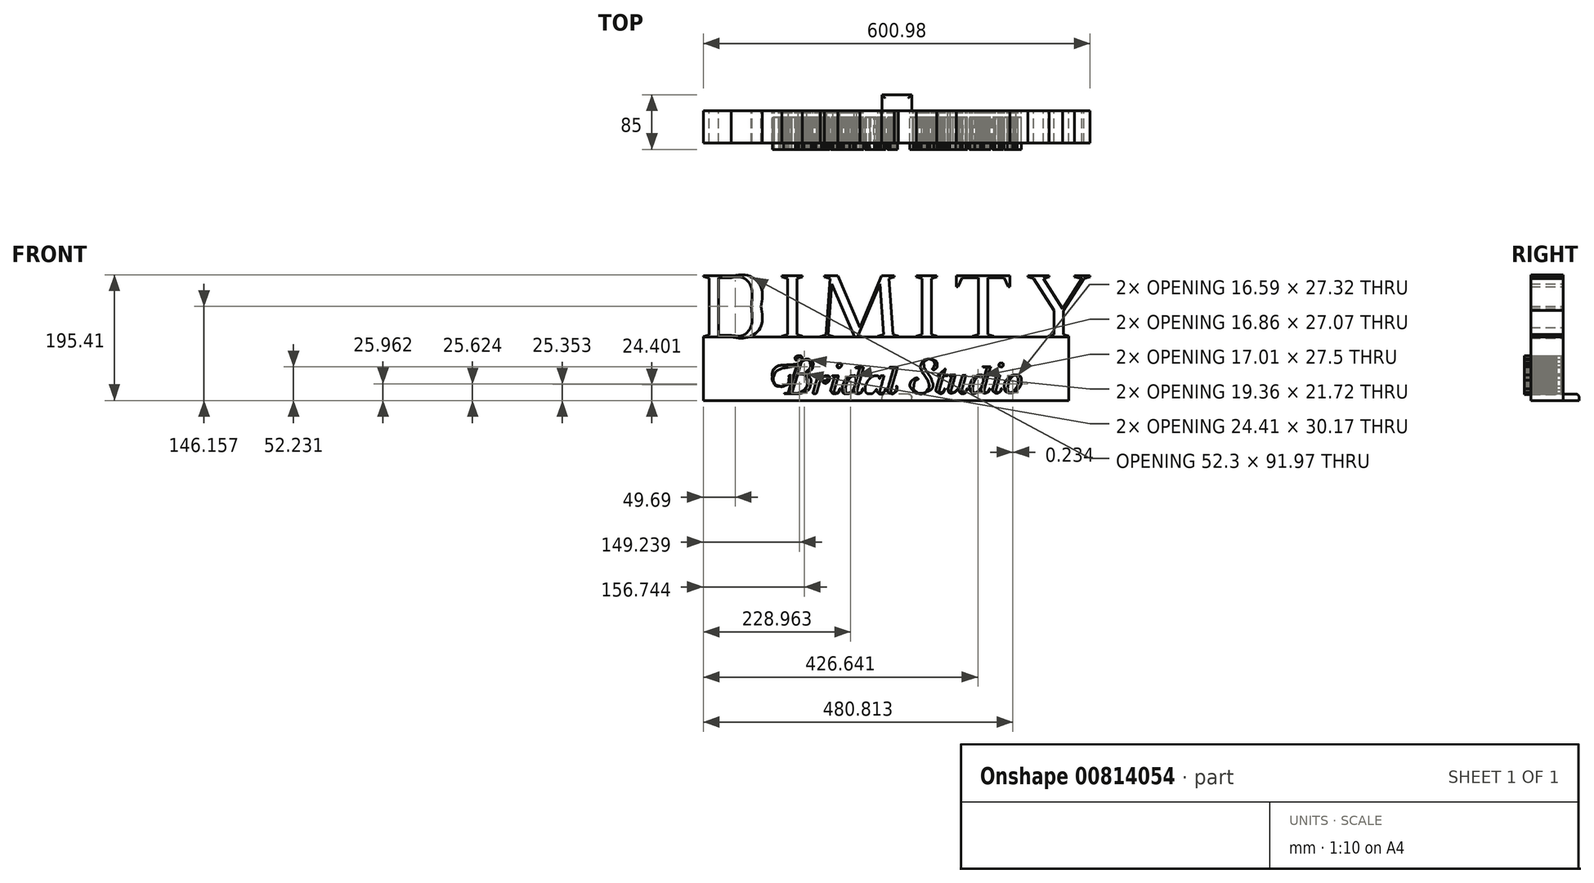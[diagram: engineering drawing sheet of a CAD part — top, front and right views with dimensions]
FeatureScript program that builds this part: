
annotation { "Feature Type Name" : "Feature", "Feature Type Description" : "" }
export const myFeature = defineFeature(function(context is Context, id is Id, definition is map)
    precondition{}
    {
        {
            var Q0;
            Q0=qCreatedBy(makeId("Front.planeOp"),FACE);
            var sketch = newSketch(context, id + "F0", { "sketchPlane" : qUnion([Q0])});
            skLineSegment(sketch, "E0", {"start": v(-300.49, 107.52) * mm, "end": v(-300.49, 106.3) * mm});
            skLineSegment(sketch, "E1", {"start": v(-300.49, 106.3) * mm, "end": v(-291.64, 104.26) * mm});
            skLineSegment(sketch, "E2", {"start": v(-291.64, 104.26) * mm, "end": v(-291.64, 15.55) * mm});
            skLineSegment(sketch, "E3", {"start": v(-291.64, 15.55) * mm, "end": v(-300.49, 13.37) * mm});
            skLineSegment(sketch, "E4", {"start": v(-300.49, 13.37) * mm, "end": v(-300.49, 12.28) * mm});
            skLineSegment(sketch, "E5", {"start": v(-300.49, 12.28) * mm, "end": v(-257.09, 12.28) * mm});
            skFitSpline(sketch, "E6", {"points": [v(-257.09, 12.28) * mm, v(-229.88, 12.28) * mm, v(-210.83, 29.97) * mm, v(-210.83, 59.9) * mm]});
            skFitSpline(sketch, "E7", {"points": [v(-210.83, 59.9) * mm, v(-210.83, 89.56) * mm, v(-229.88, 107.52) * mm, v(-257.09, 107.52) * mm]});
            skLineSegment(sketch, "E8", {"start": v(-257.09, 107.52) * mm, "end": v(-300.49, 107.52) * mm});
            skLineSegment(sketch, "E9", {"start": v(-276.95, 104.8) * mm, "end": v(-257.09, 104.8) * mm});
            skFitSpline(sketch, "E10", {"points": [v(-257.09, 104.8) * mm, v(-239.13, 104.8) * mm, v(-226.2, 89.83) * mm, v(-226.2, 59.77) * mm]});
            skFitSpline(sketch, "E11", {"points": [v(-226.2, 59.77) * mm, v(-226.2, 29.84) * mm, v(-239.13, 15) * mm, v(-257.09, 15) * mm]});
            skLineSegment(sketch, "E12", {"start": v(-257.09, 15) * mm, "end": v(-276.95, 15) * mm});
            skLineSegment(sketch, "E13", {"start": v(-276.95, 15) * mm, "end": v(-276.95, 104.8) * mm});
            skLineSegment(sketch, "E14", {"start": v(-178.44, 107.52) * mm, "end": v(-178.44, 106.16) * mm});
            skLineSegment(sketch, "E15", {"start": v(-178.44, 106.16) * mm, "end": v(-169.6, 103.58) * mm});
            skLineSegment(sketch, "E16", {"start": v(-169.6, 103.58) * mm, "end": v(-169.6, 16.23) * mm});
            skLineSegment(sketch, "E17", {"start": v(-169.6, 16.23) * mm, "end": v(-178.44, 13.64) * mm});
            skLineSegment(sketch, "E18", {"start": v(-178.44, 13.64) * mm, "end": v(-178.44, 12.28) * mm});
            skLineSegment(sketch, "E19", {"start": v(-178.44, 12.28) * mm, "end": v(-146.74, 12.28) * mm});
            skLineSegment(sketch, "E20", {"start": v(-146.74, 12.28) * mm, "end": v(-146.74, 13.64) * mm});
            skLineSegment(sketch, "E21", {"start": v(-146.74, 13.64) * mm, "end": v(-155.17, 16.23) * mm});
            skLineSegment(sketch, "E22", {"start": v(-155.17, 16.23) * mm, "end": v(-155.17, 103.58) * mm});
            skLineSegment(sketch, "E23", {"start": v(-155.17, 103.58) * mm, "end": v(-146.74, 106.16) * mm});
            skLineSegment(sketch, "E24", {"start": v(-146.74, 106.16) * mm, "end": v(-146.74, 107.52) * mm});
            skLineSegment(sketch, "E25", {"start": v(-146.74, 107.52) * mm, "end": v(-178.44, 107.52) * mm});
            skLineSegment(sketch, "E26", {"start": v(-112.18, 107.52) * mm, "end": v(-112.18, 106.16) * mm});
            skLineSegment(sketch, "E27", {"start": v(-112.18, 106.16) * mm, "end": v(-103.34, 103.58) * mm});
            skLineSegment(sketch, "E28", {"start": v(-103.34, 103.58) * mm, "end": v(-109.73, 15.96) * mm});
            skLineSegment(sketch, "E29", {"start": v(-109.73, 15.96) * mm, "end": v(-118.57, 13.37) * mm});
            skLineSegment(sketch, "E30", {"start": v(-118.57, 13.37) * mm, "end": v(-118.57, 12.28) * mm});
            skLineSegment(sketch, "E31", {"start": v(-118.57, 12.28) * mm, "end": v(-98.57, 12.28) * mm});
            skLineSegment(sketch, "E32", {"start": v(-98.57, 12.28) * mm, "end": v(-98.57, 13.37) * mm});
            skLineSegment(sketch, "E33", {"start": v(-98.57, 13.37) * mm, "end": v(-106.88, 15.96) * mm});
            skLineSegment(sketch, "E34", {"start": v(-106.88, 15.96) * mm, "end": v(-101.02, 95.14) * mm});
            skLineSegment(sketch, "E35", {"start": v(-101.02, 95.14) * mm, "end": v(-65.51, 12.28) * mm});
            skLineSegment(sketch, "E36", {"start": v(-65.51, 12.28) * mm, "end": v(-61.02, 12.28) * mm});
            skLineSegment(sketch, "E37", {"start": v(-61.02, 12.28) * mm, "end": v(-26.06, 95) * mm});
            skLineSegment(sketch, "E38", {"start": v(-26.06, 95) * mm, "end": v(-20.34, 16.23) * mm});
            skLineSegment(sketch, "E39", {"start": v(-20.34, 16.23) * mm, "end": v(-29.19, 13.64) * mm});
            skLineSegment(sketch, "E40", {"start": v(-29.19, 13.64) * mm, "end": v(-29.19, 12.28) * mm});
            skLineSegment(sketch, "E41", {"start": v(-29.19, 12.28) * mm, "end": v(2.65, 12.28) * mm});
            skLineSegment(sketch, "E42", {"start": v(2.65, 12.28) * mm, "end": v(2.65, 13.64) * mm});
            skLineSegment(sketch, "E43", {"start": v(2.65, 13.64) * mm, "end": v(-5.79, 16.23) * mm});
            skLineSegment(sketch, "E44", {"start": v(-5.79, 16.23) * mm, "end": v(-12.04, 103.58) * mm});
            skLineSegment(sketch, "E45", {"start": v(-12.04, 103.58) * mm, "end": v(-3.6, 106.16) * mm});
            skLineSegment(sketch, "E46", {"start": v(-3.6, 106.16) * mm, "end": v(-3.6, 107.52) * mm});
            skLineSegment(sketch, "E47", {"start": v(-3.6, 107.52) * mm, "end": v(-23.6, 107.52) * mm});
            skLineSegment(sketch, "E48", {"start": v(-23.6, 107.52) * mm, "end": v(-57.35, 27.25) * mm});
            skLineSegment(sketch, "E49", {"start": v(-57.35, 27.25) * mm, "end": v(-91.36, 107.52) * mm});
            skLineSegment(sketch, "E50", {"start": v(-91.36, 107.52) * mm, "end": v(-112.18, 107.52) * mm});
            skLineSegment(sketch, "E51", {"start": v(30.55, 107.52) * mm, "end": v(30.55, 106.16) * mm});
            skLineSegment(sketch, "E52", {"start": v(30.55, 106.16) * mm, "end": v(39.4, 103.58) * mm});
            skLineSegment(sketch, "E53", {"start": v(39.4, 103.58) * mm, "end": v(39.4, 16.23) * mm});
            skLineSegment(sketch, "E54", {"start": v(39.4, 16.23) * mm, "end": v(30.55, 13.64) * mm});
            skLineSegment(sketch, "E55", {"start": v(30.55, 13.64) * mm, "end": v(30.55, 12.28) * mm});
            skLineSegment(sketch, "E56", {"start": v(30.55, 12.28) * mm, "end": v(62.25, 12.28) * mm});
            skLineSegment(sketch, "E57", {"start": v(62.25, 12.28) * mm, "end": v(62.25, 13.64) * mm});
            skLineSegment(sketch, "E58", {"start": v(62.25, 13.64) * mm, "end": v(53.81, 16.23) * mm});
            skLineSegment(sketch, "E59", {"start": v(53.81, 16.23) * mm, "end": v(53.81, 103.58) * mm});
            skLineSegment(sketch, "E60", {"start": v(53.81, 103.58) * mm, "end": v(62.25, 106.16) * mm});
            skLineSegment(sketch, "E61", {"start": v(62.25, 106.16) * mm, "end": v(62.25, 107.52) * mm});
            skLineSegment(sketch, "E62", {"start": v(62.25, 107.52) * mm, "end": v(30.55, 107.52) * mm});
            skLineSegment(sketch, "E63", {"start": v(93, 107.52) * mm, "end": v(93, 90.79) * mm});
            skLineSegment(sketch, "E64", {"start": v(93, 90.79) * mm, "end": v(95.17, 90.79) * mm});
            skLineSegment(sketch, "E65", {"start": v(95.17, 90.79) * mm, "end": v(101.57, 104.8) * mm});
            skLineSegment(sketch, "E66", {"start": v(101.57, 104.8) * mm, "end": v(126.88, 104.8) * mm});
            skLineSegment(sketch, "E67", {"start": v(126.88, 104.8) * mm, "end": v(126.88, 16.23) * mm});
            skLineSegment(sketch, "E68", {"start": v(126.88, 16.23) * mm, "end": v(118.03, 13.64) * mm});
            skLineSegment(sketch, "E69", {"start": v(118.03, 13.64) * mm, "end": v(118.03, 12.28) * mm});
            skLineSegment(sketch, "E70", {"start": v(118.03, 12.28) * mm, "end": v(150.41, 12.28) * mm});
            skLineSegment(sketch, "E71", {"start": v(150.41, 12.28) * mm, "end": v(150.41, 13.64) * mm});
            skLineSegment(sketch, "E72", {"start": v(150.41, 13.64) * mm, "end": v(141.57, 16.23) * mm});
            skLineSegment(sketch, "E73", {"start": v(141.57, 16.23) * mm, "end": v(141.57, 104.8) * mm});
            skLineSegment(sketch, "E74", {"start": v(141.57, 104.8) * mm, "end": v(167.01, 104.8) * mm});
            skLineSegment(sketch, "E75", {"start": v(167.01, 104.8) * mm, "end": v(173.27, 90.79) * mm});
            skLineSegment(sketch, "E76", {"start": v(173.27, 90.79) * mm, "end": v(175.58, 90.79) * mm});
            skLineSegment(sketch, "E77", {"start": v(175.58, 90.79) * mm, "end": v(175.58, 107.52) * mm});
            skLineSegment(sketch, "E78", {"start": v(175.58, 107.52) * mm, "end": v(93, 107.52) * mm});
            skLineSegment(sketch, "E79", {"start": v(204.16, 107.52) * mm, "end": v(204.16, 106.16) * mm});
            skLineSegment(sketch, "E80", {"start": v(204.16, 106.16) * mm, "end": v(212.6, 103.58) * mm});
            skLineSegment(sketch, "E81", {"start": v(212.6, 103.58) * mm, "end": v(244.43, 53.64) * mm});
            skLineSegment(sketch, "E82", {"start": v(244.43, 53.64) * mm, "end": v(244.43, 16.23) * mm});
            skLineSegment(sketch, "E83", {"start": v(244.43, 16.23) * mm, "end": v(235.6, 13.64) * mm});
            skLineSegment(sketch, "E84", {"start": v(235.6, 13.64) * mm, "end": v(235.6, 12.28) * mm});
            skLineSegment(sketch, "E85", {"start": v(235.6, 12.28) * mm, "end": v(267.43, 12.28) * mm});
            skLineSegment(sketch, "E86", {"start": v(267.43, 12.28) * mm, "end": v(267.43, 13.64) * mm});
            skLineSegment(sketch, "E87", {"start": v(267.43, 13.64) * mm, "end": v(259, 16.23) * mm});
            skLineSegment(sketch, "E88", {"start": v(259, 16.23) * mm, "end": v(259, 53.64) * mm});
            skLineSegment(sketch, "E89", {"start": v(259, 53.64) * mm, "end": v(290.83, 103.58) * mm});
            skLineSegment(sketch, "E90", {"start": v(290.83, 103.58) * mm, "end": v(300.49, 106.16) * mm});
            skLineSegment(sketch, "E91", {"start": v(300.49, 106.16) * mm, "end": v(300.49, 107.52) * mm});
            skLineSegment(sketch, "E92", {"start": v(300.49, 107.52) * mm, "end": v(276.27, 107.52) * mm});
            skLineSegment(sketch, "E93", {"start": v(276.27, 107.52) * mm, "end": v(276.27, 106.16) * mm});
            skLineSegment(sketch, "E94", {"start": v(276.27, 106.16) * mm, "end": v(287.7, 103.58) * mm});
            skLineSegment(sketch, "E95", {"start": v(287.7, 103.58) * mm, "end": v(257.63, 56.64) * mm});
            skLineSegment(sketch, "E96", {"start": v(257.63, 56.64) * mm, "end": v(227.97, 103.58) * mm});
            skLineSegment(sketch, "E97", {"start": v(227.97, 103.58) * mm, "end": v(236.95, 106.16) * mm});
            skLineSegment(sketch, "E98", {"start": v(236.95, 106.16) * mm, "end": v(236.95, 107.52) * mm});
            skLineSegment(sketch, "E99", {"start": v(236.95, 107.52) * mm, "end": v(204.16, 107.52) * mm});
            skFitSpline(sketch, "E100", {"points": [v(-152.8, -16.98) * mm, v(-153.04, -17) * mm, v(-153.29, -17.01) * mm, v(-153.54, -17.05) * mm]});
            skFitSpline(sketch, "E101", {"points": [v(-153.54, -17.05) * mm, v(-156.18, -17.4) * mm, v(-157.9, -19.88) * mm, v(-157.32, -22.49) * mm]});
            skFitSpline(sketch, "E102", {"points": [v(-157.32, -22.49) * mm, v(-157.17, -23.17) * mm, v(-156.84, -23.7) * mm, v(-156.02, -23.97) * mm]});
            skFitSpline(sketch, "E103", {"points": [v(-156.02, -23.97) * mm, v(-155.76, -23.3) * mm, v(-155.5, -22.7) * mm, v(-155.27, -22.1) * mm]});
            skFitSpline(sketch, "E104", {"points": [v(-155.27, -22.1) * mm, v(-154.62, -20.46) * mm, v(-153.4, -19.45) * mm, v(-151.72, -19.03) * mm]});
            skFitSpline(sketch, "E105", {"points": [v(-151.72, -19.03) * mm, v(-150.18, -18.63) * mm, v(-148.46, -19.17) * mm, v(-147.61, -21.44) * mm]});
            skFitSpline(sketch, "E106", {"points": [v(-147.61, -21.44) * mm, v(-147.29, -22.6) * mm, v(-147.43, -23.05) * mm, v(-147.61, -23.61) * mm]});
            skFitSpline(sketch, "E107", {"points": [v(-147.61, -23.61) * mm, v(-148.32, -25.33) * mm, v(-149.28, -26.65) * mm, v(-150.77, -27.59) * mm]});
            skFitSpline(sketch, "E108", {"points": [v(-150.77, -27.59) * mm, v(-152.75, -28.84) * mm, v(-154.93, -29.6) * mm, v(-157.2, -29.9) * mm]});
            skFitSpline(sketch, "E109", {"points": [v(-157.2, -29.9) * mm, v(-160.75, -30.36) * mm, v(-164.33, -30.69) * mm, v(-167.9, -30.82) * mm]});
            skFitSpline(sketch, "E110", {"points": [v(-167.9, -30.82) * mm, v(-170.73, -30.92) * mm, v(-173.52, -31.26) * mm, v(-176.32, -31.64) * mm]});
            skFitSpline(sketch, "E111", {"points": [v(-176.32, -31.64) * mm, v(-185.34, -32.84) * mm, v(-192.7, -40.76) * mm, v(-193.3, -49.28) * mm]});
            skFitSpline(sketch, "E112", {"points": [v(-193.3, -49.28) * mm, v(-193.53, -52.42) * mm, v(-193.13, -55.38) * mm, v(-191.65, -58.16) * mm]});
            skFitSpline(sketch, "E113", {"points": [v(-191.65, -58.16) * mm, v(-189.52, -62.19) * mm, v(-186.07, -64.19) * mm, v(-181.6, -64.51) * mm]});
            skFitSpline(sketch, "E114", {"points": [v(-181.6, -64.51) * mm, v(-178.73, -64.72) * mm, v(-175.97, -64.25) * mm, v(-173.32, -63.13) * mm]});
            skFitSpline(sketch, "E115", {"points": [v(-173.32, -63.13) * mm, v(-169.2, -61.37) * mm, v(-165.98, -58.67) * mm, v(-164.2, -54.46) * mm]});
            skFitSpline(sketch, "E116", {"points": [v(-164.2, -54.46) * mm, v(-163.5, -52.79) * mm, v(-163.26, -51.04) * mm, v(-163.84, -49.28) * mm]});
            skFitSpline(sketch, "E117", {"points": [v(-163.84, -49.28) * mm, v(-164.45, -47.46) * mm, v(-166.05, -46.95) * mm, v(-167.88, -48.07) * mm]});
            skFitSpline(sketch, "E118", {"points": [v(-167.88, -48.07) * mm, v(-167.12, -49.52) * mm, v(-167.24, -51.02) * mm, v(-167.36, -52.49) * mm]});
            skFitSpline(sketch, "E119", {"points": [v(-167.36, -52.49) * mm, v(-167.76, -57.27) * mm, v(-170.1, -60.76) * mm, v(-174.54, -62.72) * mm]});
            skFitSpline(sketch, "E120", {"points": [v(-174.54, -62.72) * mm, v(-177.39, -63.97) * mm, v(-180.37, -64.22) * mm, v(-183.39, -63.54) * mm]});
            skFitSpline(sketch, "E121", {"points": [v(-183.39, -63.54) * mm, v(-186.2, -62.9) * mm, v(-188.52, -61.45) * mm, v(-189.98, -58.87) * mm]});
            skFitSpline(sketch, "E122", {"points": [v(-189.98, -58.87) * mm, v(-191.95, -55.34) * mm, v(-192.08, -51.59) * mm, v(-190.71, -47.9) * mm]});
            skFitSpline(sketch, "E123", {"points": [v(-190.71, -47.9) * mm, v(-188.8, -42.75) * mm, v(-184.98, -39.31) * mm, v(-179.95, -37.17) * mm]});
            skFitSpline(sketch, "E124", {"points": [v(-179.95, -37.17) * mm, v(-176.52, -35.71) * mm, v(-172.82, -35.4) * mm, v(-169.22, -34.7) * mm]});
            skFitSpline(sketch, "E125", {"points": [v(-169.22, -34.7) * mm, v(-164.8, -33.83) * mm, v(-160.41, -32.95) * mm, v(-156.21, -31.29) * mm]});
            skFitSpline(sketch, "E126", {"points": [v(-156.21, -31.29) * mm, v(-155.8, -31.12) * mm, v(-155.35, -31.04) * mm, v(-154.74, -30.87) * mm]});
            skFitSpline(sketch, "E127", {"points": [v(-154.74, -30.87) * mm, v(-159.45, -45.8) * mm, v(-164.09, -60.51) * mm, v(-168.77, -75.36) * mm]});
            skFitSpline(sketch, "E128", {"points": [v(-168.77, -75.36) * mm, v(-169.81, -75.36) * mm, v(-170.81, -75.32) * mm, v(-171.8, -75.38) * mm]});
            skFitSpline(sketch, "E129", {"points": [v(-171.8, -75.38) * mm, v(-172.77, -75.43) * mm, v(-173.8, -75.1) * mm, v(-174.7, -75.79) * mm]});
            skFitSpline(sketch, "E130", {"points": [v(-174.7, -75.79) * mm, v(-174.18, -75.97) * mm, v(-173.67, -76) * mm, v(-173.16, -76) * mm]});
            skFitSpline(sketch, "E131", {"points": [v(-173.16, -76) * mm, v(-167.7, -76.01) * mm, v(-162.24, -76) * mm, v(-156.78, -76.01) * mm]});
            skFitSpline(sketch, "E132", {"points": [v(-156.78, -76.01) * mm, v(-154.43, -76.02) * mm, v(-152.1, -75.82) * mm, v(-149.84, -75.16) * mm]});
            skFitSpline(sketch, "E133", {"points": [v(-149.84, -75.16) * mm, v(-141.45, -72.71) * mm, v(-135.78, -67.59) * mm, v(-133.9, -58.82) * mm]});
            skFitSpline(sketch, "E134", {"points": [v(-133.9, -58.82) * mm, v(-133.28, -55.91) * mm, v(-133.76, -53.07) * mm, v(-135.3, -50.52) * mm]});
            skFitSpline(sketch, "E135", {"points": [v(-135.3, -50.52) * mm, v(-137.03, -47.7) * mm, v(-139.64, -46) * mm, v(-142.84, -45.2) * mm]});
            skFitSpline(sketch, "E136", {"points": [v(-142.84, -45.2) * mm, v(-143.45, -45.04) * mm, v(-144.06, -44.9) * mm, v(-144.67, -44.77) * mm]});
            skFitSpline(sketch, "E137", {"points": [v(-144.67, -44.77) * mm, v(-141.88, -43.95) * mm, v(-139.26, -42.96) * mm, v(-136.88, -41.38) * mm]});
            skFitSpline(sketch, "E138", {"points": [v(-136.88, -41.38) * mm, v(-133.53, -39.16) * mm, v(-131.03, -36.29) * mm, v(-130.38, -32.18) * mm]});
            skFitSpline(sketch, "E139", {"points": [v(-130.38, -32.18) * mm, v(-129.9, -29.15) * mm, v(-130.78, -26.47) * mm, v(-133.28, -24.68) * mm]});
            skFitSpline(sketch, "E140", {"points": [v(-133.28, -24.68) * mm, v(-136.8, -22.14) * mm, v(-140.67, -21.79) * mm, v(-144.66, -23.69) * mm]});
            skFitSpline(sketch, "E141", {"points": [v(-144.66, -23.69) * mm, v(-145.54, -24.11) * mm, v(-146.4, -24.6) * mm, v(-147.48, -25.19) * mm]});
            skFitSpline(sketch, "E142", {"points": [v(-147.48, -25.19) * mm, v(-147.29, -24.26) * mm, v(-147, -23.57) * mm, v(-147.02, -22.9) * mm]});
            skFitSpline(sketch, "E143", {"points": [v(-147.02, -22.9) * mm, v(-147.1, -19.5) * mm, v(-149.24, -16.86) * mm, v(-152.8, -16.98) * mm]});
            skFitSpline(sketch, "E144", {"points": [v(-140.4, -23.23) * mm, v(-138.6, -23.18) * mm, v(-136.97, -23.72) * mm, v(-135.77, -25.27) * mm]});
            skFitSpline(sketch, "E145", {"points": [v(-135.77, -25.27) * mm, v(-134.92, -26.38) * mm, v(-134.4, -27.67) * mm, v(-134.35, -29.1) * mm]});
            skFitSpline(sketch, "E146", {"points": [v(-134.35, -29.1) * mm, v(-134.2, -33.85) * mm, v(-136.18, -37.66) * mm, v(-139.72, -40.64) * mm]});
            skFitSpline(sketch, "E147", {"points": [v(-139.72, -40.64) * mm, v(-143.58, -43.88) * mm, v(-148.18, -44.9) * mm, v(-153.12, -44.56) * mm]});
            skFitSpline(sketch, "E148", {"points": [v(-153.12, -44.56) * mm, v(-153.21, -44.56) * mm, v(-153.3, -44.48) * mm, v(-153.37, -44.44) * mm]});
            skFitSpline(sketch, "E149", {"points": [v(-153.37, -44.44) * mm, v(-153.4, -43.57) * mm, v(-149.33, -30.3) * mm, v(-147.86, -26.5) * mm]});
            skFitSpline(sketch, "E150", {"points": [v(-147.86, -26.5) * mm, v(-145.91, -24.95) * mm, v(-143.76, -23.6) * mm, v(-141.17, -23.3) * mm]});
            skFitSpline(sketch, "E151", {"points": [v(-141.17, -23.3) * mm, v(-140.9, -23.26) * mm, v(-140.65, -23.24) * mm, v(-140.4, -23.23) * mm]});
            skFitSpline(sketch, "E152", {"points": [v(-153.88, -45.22) * mm, v(-151.95, -45.22) * mm, v(-150.28, -45.2) * mm, v(-148.6, -45.23) * mm]});
            skFitSpline(sketch, "E153", {"points": [v(-148.6, -45.23) * mm, v(-146.96, -45.25) * mm, v(-145.36, -45.59) * mm, v(-143.94, -46.44) * mm]});
            skFitSpline(sketch, "E154", {"points": [v(-143.94, -46.44) * mm, v(-141.03, -48.17) * mm, v(-139.6, -50.88) * mm, v(-139.5, -54.17) * mm]});
            skFitSpline(sketch, "E155", {"points": [v(-139.5, -54.17) * mm, v(-139.28, -62.4) * mm, v(-142.76, -68.75) * mm, v(-149.69, -73.16) * mm]});
            skFitSpline(sketch, "E156", {"points": [v(-149.69, -73.16) * mm, v(-151.47, -74.3) * mm, v(-153.5, -74.94) * mm, v(-155.63, -75.1) * mm]});
            skFitSpline(sketch, "E157", {"points": [v(-155.63, -75.1) * mm, v(-157.96, -75.26) * mm, v(-160.3, -75.28) * mm, v(-162.64, -75.36) * mm]});
            skFitSpline(sketch, "E158", {"points": [v(-162.64, -75.36) * mm, v(-162.87, -75.37) * mm, v(-163.1, -75.32) * mm, v(-163.46, -75.28) * mm]});
            skFitSpline(sketch, "E159", {"points": [v(-163.46, -75.28) * mm, v(-160.24, -65.2) * mm, v(-157.06, -55.2) * mm, v(-153.88, -45.22) * mm]});
            skFitSpline(sketch, "E160", {"points": [v(-99.44, -47.87) * mm, v(-99.88, -47.87) * mm, v(-100.28, -47.98) * mm, v(-100.5, -48.7) * mm]});
            skLineSegment(sketch, "E161", {"start": v(-100.5, -48.7) * mm, "end": v(-93.9, -48.7) * mm});
            skFitSpline(sketch, "E162", {"points": [v(-93.9, -48.7) * mm, v(-95.68, -49.47) * mm, v(-96.86, -50.7) * mm, v(-97.49, -52.48) * mm]});
            skFitSpline(sketch, "E163", {"points": [v(-97.49, -52.48) * mm, v(-97.7, -53.06) * mm, v(-97.9, -53.65) * mm, v(-98.08, -54.24) * mm]});
            skFitSpline(sketch, "E164", {"points": [v(-98.08, -54.24) * mm, v(-98.86, -56.95) * mm, v(-99.63, -59.66) * mm, v(-100.41, -62.36) * mm]});
            skFitSpline(sketch, "E165", {"points": [v(-100.41, -62.36) * mm, v(-101.03, -64.52) * mm, v(-101.69, -66.67) * mm, v(-102.26, -68.84) * mm]});
            skFitSpline(sketch, "E166", {"points": [v(-102.26, -68.84) * mm, v(-102.67, -70.4) * mm, v(-102.45, -71.92) * mm, v(-101.37, -73.17) * mm]});
            skFitSpline(sketch, "E167", {"points": [v(-101.37, -73.17) * mm, v(-99.47, -75.34) * mm, v(-97, -76.05) * mm, v(-94.24, -75.45) * mm]});
            skFitSpline(sketch, "E168", {"points": [v(-94.24, -75.45) * mm, v(-91.39, -74.84) * mm, v(-89.87, -72.71) * mm, v(-88.85, -70.17) * mm]});
            skFitSpline(sketch, "E169", {"points": [v(-88.85, -70.17) * mm, v(-88.56, -69.45) * mm, v(-88.45, -68.66) * mm, v(-88.19, -67.63) * mm]});
            skFitSpline(sketch, "E170", {"points": [v(-88.19, -67.63) * mm, v(-89.05, -68.35) * mm, v(-89, -68.37) * mm, v(-89.2, -69.1) * mm]});
            skFitSpline(sketch, "E171", {"points": [v(-89.2, -69.1) * mm, v(-90.03, -71.83) * mm, v(-91.43, -74.05) * mm, v(-94.44, -74.82) * mm]});
            skFitSpline(sketch, "E172", {"points": [v(-94.44, -74.82) * mm, v(-96.33, -75.3) * mm, v(-97.52, -74.53) * mm, v(-97.45, -72.6) * mm]});
            skFitSpline(sketch, "E173", {"points": [v(-97.45, -72.6) * mm, v(-97.4, -71.27) * mm, v(-97.13, -69.94) * mm, v(-96.8, -68.65) * mm]});
            skFitSpline(sketch, "E174", {"points": [v(-96.8, -68.65) * mm, v(-96.08, -65.98) * mm, v(-95.24, -63.34) * mm, v(-94.47, -60.68) * mm]});
            skFitSpline(sketch, "E175", {"points": [v(-94.47, -60.68) * mm, v(-93.4, -56.96) * mm, v(-90.74, -47.92) * mm, v(-90.82, -47.92) * mm]});
            skFitSpline(sketch, "E176", {"points": [v(-90.82, -47.92) * mm, v(-93.45, -47.9) * mm, v(-96.8, -47.88) * mm, v(-99.44, -47.87) * mm]});
            skFitSpline(sketch, "E177", {"points": [v(-89.18, -29.1) * mm, v(-90.92, -29.16) * mm, v(-92.45, -31.19) * mm, v(-92.4, -32.52) * mm]});
            skFitSpline(sketch, "E178", {"points": [v(-92.4, -32.52) * mm, v(-92.32, -34.27) * mm, v(-90.7, -35.55) * mm, v(-89.03, -35.07) * mm]});
            skFitSpline(sketch, "E179", {"points": [v(-89.03, -35.07) * mm, v(-87.86, -34.74) * mm, v(-86.96, -34) * mm, v(-86.51, -32.88) * mm]});
            skFitSpline(sketch, "E180", {"points": [v(-86.51, -32.88) * mm, v(-85.65, -30.73) * mm, v(-87.2, -28.92) * mm, v(-88.83, -29.1) * mm]});
            skFitSpline(sketch, "E181", {"points": [v(-88.83, -29.1) * mm, v(-88.95, -29.1) * mm, v(-89.06, -29.09) * mm, v(-89.18, -29.1) * mm]});
            skFitSpline(sketch, "E182", {"points": [v(-109.1, -47.68) * mm, v(-110.54, -47.63) * mm, v(-111.89, -48.02) * mm, v(-113.14, -48.77) * mm]});
            skFitSpline(sketch, "E183", {"points": [v(-113.14, -48.77) * mm, v(-115.58, -50.23) * mm, v(-117.38, -52.3) * mm, v(-119.1, -54.64) * mm]});
            skFitSpline(sketch, "E184", {"points": [v(-119.1, -54.64) * mm, v(-118.5, -52.46) * mm, v(-117.9, -50.28) * mm, v(-117.27, -47.95) * mm]});
            skFitSpline(sketch, "E185", {"points": [v(-117.27, -47.95) * mm, v(-117.97, -47.9) * mm, v(-124.98, -47.84) * mm, v(-125.9, -47.84) * mm]});
            skFitSpline(sketch, "E186", {"points": [v(-125.9, -47.84) * mm, v(-126.34, -47.84) * mm, v(-126.75, -47.95) * mm, v(-126.98, -48.67) * mm]});
            skFitSpline(sketch, "E187", {"points": [v(-126.98, -48.67) * mm, v(-126.85, -48.67) * mm, v(-122.61, -48.67) * mm, v(-120.6, -48.67) * mm]});
            skFitSpline(sketch, "E188", {"points": [v(-120.6, -48.67) * mm, v(-122.7, -49.78) * mm, v(-123.7, -51.55) * mm, v(-124.3, -53.66) * mm]});
            skFitSpline(sketch, "E189", {"points": [v(-124.3, -53.66) * mm, v(-125.9, -59.36) * mm, v(-127.54, -65.06) * mm, v(-129.16, -70.76) * mm]});
            skFitSpline(sketch, "E190", {"points": [v(-129.16, -70.76) * mm, v(-129.58, -72.22) * mm, v(-129.97, -73.68) * mm, v(-130.37, -75.12) * mm]});
            skFitSpline(sketch, "E191", {"points": [v(-130.37, -75.12) * mm, v(-129.09, -75.58) * mm, v(-126.2, -75.58) * mm, v(-124.98, -75.16) * mm]});
            skFitSpline(sketch, "E192", {"points": [v(-124.98, -75.16) * mm, v(-124.9, -74.94) * mm, v(-124.78, -74.68) * mm, v(-124.7, -74.4) * mm]});
            skFitSpline(sketch, "E193", {"points": [v(-124.7, -74.4) * mm, v(-123.86, -71.52) * mm, v(-123.04, -68.62) * mm, v(-122.2, -65.73) * mm]});
            skFitSpline(sketch, "E194", {"points": [v(-122.2, -65.73) * mm, v(-121.32, -62.71) * mm, v(-120.61, -59.64) * mm, v(-119.16, -56.8) * mm]});
            skFitSpline(sketch, "E195", {"points": [v(-119.16, -56.8) * mm, v(-117.89, -54.28) * mm, v(-116.27, -52.06) * mm, v(-114.1, -50.27) * mm]});
            skFitSpline(sketch, "E196", {"points": [v(-114.1, -50.27) * mm, v(-112.56, -48.98) * mm, v(-110.78, -48.2) * mm, v(-108.69, -48.41) * mm]});
            skFitSpline(sketch, "E197", {"points": [v(-108.69, -48.41) * mm, v(-107.74, -48.5) * mm, v(-107.23, -48.81) * mm, v(-107.07, -49.56) * mm]});
            skFitSpline(sketch, "E198", {"points": [v(-107.07, -49.56) * mm, v(-106.88, -50.46) * mm, v(-106.88, -51.37) * mm, v(-107.37, -52.2) * mm]});
            skFitSpline(sketch, "E199", {"points": [v(-107.37, -52.2) * mm, v(-108.52, -54.16) * mm, v(-110.17, -55.3) * mm, v(-112.5, -55.3) * mm]});
            skFitSpline(sketch, "E200", {"points": [v(-112.5, -55.3) * mm, v(-113.06, -55.31) * mm, v(-113.62, -55.3) * mm, v(-114.11, -55.3) * mm]});
            skFitSpline(sketch, "E201", {"points": [v(-114.11, -55.3) * mm, v(-114.66, -57.08) * mm, v(-113.97, -58.56) * mm, v(-112.45, -59.04) * mm]});
            skFitSpline(sketch, "E202", {"points": [v(-112.45, -59.04) * mm, v(-110.55, -59.63) * mm, v(-108.85, -59.06) * mm, v(-107.39, -57.83) * mm]});
            skFitSpline(sketch, "E203", {"points": [v(-107.39, -57.83) * mm, v(-105.55, -56.28) * mm, v(-104.76, -54.18) * mm, v(-104.73, -51.85) * mm]});
            skFitSpline(sketch, "E204", {"points": [v(-104.73, -51.85) * mm, v(-104.7, -49.6) * mm, v(-106.22, -48) * mm, v(-108.49, -47.73) * mm]});
            skFitSpline(sketch, "E205", {"points": [v(-108.49, -47.73) * mm, v(-108.7, -47.7) * mm, v(-108.9, -47.69) * mm, v(-109.1, -47.68) * mm]});
            skFitSpline(sketch, "E206", {"points": [v(-10.23, -34.75) * mm, v(-10.66, -34.75) * mm, v(-11.07, -34.87) * mm, v(-11.3, -35.59) * mm]});
            skLineSegment(sketch, "E207", {"start": v(-11.3, -35.59) * mm, "end": v(-4.1, -35.59) * mm});
            skFitSpline(sketch, "E208", {"points": [v(-4.1, -35.59) * mm, v(-3.97, -35.6) * mm, v(-3.84, -35.6) * mm, v(-3.7, -35.6) * mm]});
            skFitSpline(sketch, "E209", {"points": [v(-3.7, -35.6) * mm, v(-5.22, -37.28) * mm, v(-5.84, -39.27) * mm, v(-6.32, -41.33) * mm]});
            skFitSpline(sketch, "E210", {"points": [v(-6.32, -41.33) * mm, v(-6.4, -41.65) * mm, v(-6.48, -41.97) * mm, v(-6.57, -42.3) * mm]});
            skFitSpline(sketch, "E211", {"points": [v(-6.57, -42.3) * mm, v(-8.8, -49.96) * mm, v(-11.04, -57.62) * mm, v(-13.23, -65.3) * mm]});
            skFitSpline(sketch, "E212", {"points": [v(-13.23, -65.3) * mm, v(-13.7, -66.98) * mm, v(-14.38, -68.63) * mm, v(-14.26, -70.46) * mm]});
            skFitSpline(sketch, "E213", {"points": [v(-14.26, -70.46) * mm, v(-14.15, -72.25) * mm, v(-13.39, -73.6) * mm, v(-11.84, -74.43) * mm]});
            skFitSpline(sketch, "E214", {"points": [v(-11.84, -74.43) * mm, v(-10.97, -74.9) * mm, v(-9.99, -75.18) * mm, v(-9.03, -75.46) * mm]});
            skFitSpline(sketch, "E215", {"points": [v(-9.03, -75.46) * mm, v(-6.92, -76.1) * mm, v(-4.97, -75.52) * mm, v(-3.4, -74.15) * mm]});
            skFitSpline(sketch, "E216", {"points": [v(-3.4, -74.15) * mm, v(-0.63, -71.74) * mm, v(0.5, -68.56) * mm, v(0.17, -64.9) * mm]});
            skFitSpline(sketch, "E217", {"points": [v(0.17, -64.9) * mm, v(0.14, -64.58) * mm, v(-0.08, -64.29) * mm, v(-0.2, -63.98) * mm]});
            skFitSpline(sketch, "E218", {"points": [v(-0.2, -63.98) * mm, v(-0.3, -64) * mm, v(-0.4, -64.03) * mm, v(-0.5, -64.05) * mm]});
            skFitSpline(sketch, "E219", {"points": [v(-0.5, -64.05) * mm, v(-0.54, -64.25) * mm, v(-0.68, -64.49) * mm, v(-0.63, -64.67) * mm]});
            skFitSpline(sketch, "E220", {"points": [v(-0.63, -64.67) * mm, v(-0.03, -66.9) * mm, v(-0.7, -68.95) * mm, v(-1.67, -70.9) * mm]});
            skFitSpline(sketch, "E221", {"points": [v(-1.67, -70.9) * mm, v(-2.7, -72.94) * mm, v(-4.25, -74.44) * mm, v(-6.6, -74.93) * mm]});
            skFitSpline(sketch, "E222", {"points": [v(-6.6, -74.93) * mm, v(-8.06, -75.23) * mm, v(-9.2, -74.44) * mm, v(-9.3, -72.97) * mm]});
            skFitSpline(sketch, "E223", {"points": [v(-9.3, -72.97) * mm, v(-9.4, -71.62) * mm, v(-9.23, -70.31) * mm, v(-8.84, -69) * mm]});
            skFitSpline(sketch, "E224", {"points": [v(-8.84, -69) * mm, v(-7.22, -63.46) * mm, v(-5.64, -57.9) * mm, v(-4.04, -52.34) * mm]});
            skFitSpline(sketch, "E225", {"points": [v(-4.04, -52.34) * mm, v(-2.68, -47.61) * mm, v(0.9, -34.98) * mm, v(1.12, -34.78) * mm]});
            skFitSpline(sketch, "E226", {"points": [v(1.12, -34.78) * mm, v(-0.02, -34.77) * mm, v(-9.08, -34.76) * mm, v(-10.23, -34.75) * mm]});
            skFitSpline(sketch, "E227", {"points": [v(51.06, -21.7) * mm, v(49.79, -21.7) * mm, v(48.5, -21.87) * mm, v(47.2, -22.19) * mm]});
            skFitSpline(sketch, "E228", {"points": [v(47.2, -22.19) * mm, v(42.8, -23.28) * mm, v(39.62, -25.86) * mm, v(37.88, -30.15) * mm]});
            skFitSpline(sketch, "E229", {"points": [v(37.88, -30.15) * mm, v(36.52, -33.53) * mm, v(37.16, -36.73) * mm, v(38.6, -39.87) * mm]});
            skFitSpline(sketch, "E230", {"points": [v(38.6, -39.87) * mm, v(40.18, -43.33) * mm, v(42.47, -46.35) * mm, v(44.57, -49.5) * mm]});
            skFitSpline(sketch, "E231", {"points": [v(44.57, -49.5) * mm, v(46.38, -52.2) * mm, v(48.13, -54.96) * mm, v(49.07, -58.11) * mm]});
            skFitSpline(sketch, "E232", {"points": [v(49.07, -58.11) * mm, v(50.33, -62.34) * mm, v(49.96, -66.33) * mm, v(47.16, -69.92) * mm]});
            skFitSpline(sketch, "E233", {"points": [v(47.16, -69.92) * mm, v(43.36, -74.8) * mm, v(35.54, -75.94) * mm, v(30.4, -72.7) * mm]});
            skFitSpline(sketch, "E234", {"points": [v(30.4, -72.7) * mm, v(27.57, -70.9) * mm, v(26, -68.34) * mm, v(26.13, -64.91) * mm]});
            skFitSpline(sketch, "E235", {"points": [v(26.13, -64.91) * mm, v(26.18, -63.82) * mm, v(26.23, -62.7) * mm, v(26.51, -61.65) * mm]});
            skFitSpline(sketch, "E236", {"points": [v(26.51, -61.65) * mm, v(27.44, -58.16) * mm, v(29.01, -55.12) * mm, v(32.59, -53.62) * mm]});
            skFitSpline(sketch, "E237", {"points": [v(32.59, -53.62) * mm, v(32.8, -53.53) * mm, v(32.97, -53.35) * mm, v(33.14, -53.22) * mm]});
            skFitSpline(sketch, "E238", {"points": [v(33.14, -53.22) * mm, v(32.42, -51.77) * mm, v(31.36, -51.2) * mm, v(29.89, -51.5) * mm]});
            skFitSpline(sketch, "E239", {"points": [v(29.89, -51.5) * mm, v(28.35, -51.8) * mm, v(27, -52.5) * mm, v(25.85, -53.57) * mm]});
            skFitSpline(sketch, "E240", {"points": [v(25.85, -53.57) * mm, v(21.8, -57.33) * mm, v(20.5, -64.52) * mm, v(24.44, -69.5) * mm]});
            skFitSpline(sketch, "E241", {"points": [v(24.44, -69.5) * mm, v(28.02, -74.02) * mm, v(32.9, -75.35) * mm, v(38.36, -75.06) * mm]});
            skFitSpline(sketch, "E242", {"points": [v(38.36, -75.06) * mm, v(41.39, -74.9) * mm, v(44.29, -74.03) * mm, v(46.96, -72.53) * mm]});
            skFitSpline(sketch, "E243", {"points": [v(46.96, -72.53) * mm, v(53.54, -68.82) * mm, v(56.49, -62.86) * mm, v(54.23, -55.22) * mm]});
            skFitSpline(sketch, "E244", {"points": [v(54.23, -55.22) * mm, v(53.3, -52.11) * mm, v(51.7, -49.35) * mm, v(49.96, -46.66) * mm]});
            skFitSpline(sketch, "E245", {"points": [v(49.96, -46.66) * mm, v(48.09, -43.77) * mm, v(46.16, -40.9) * mm, v(44.35, -37.98) * mm]});
            skFitSpline(sketch, "E246", {"points": [v(44.35, -37.98) * mm, v(43.11, -35.97) * mm, v(42.24, -33.8) * mm, v(42.07, -31.4) * mm]});
            skFitSpline(sketch, "E247", {"points": [v(42.07, -31.4) * mm, v(41.85, -28.22) * mm, v(42.69, -25.43) * mm, v(45.6, -23.78) * mm]});
            skFitSpline(sketch, "E248", {"points": [v(45.6, -23.78) * mm, v(48.58, -22.06) * mm, v(51.78, -21.98) * mm, v(54.99, -23.26) * mm]});
            skFitSpline(sketch, "E249", {"points": [v(54.99, -23.26) * mm, v(55.99, -23.66) * mm, v(56.74, -24.42) * mm, v(57.24, -25.38) * mm]});
            skFitSpline(sketch, "E250", {"points": [v(57.24, -25.38) * mm, v(58.78, -28.37) * mm, v(58.66, -31.39) * mm, v(57.26, -34.36) * mm]});
            skFitSpline(sketch, "E251", {"points": [v(57.26, -34.36) * mm, v(56.75, -35.42) * mm, v(56, -36.36) * mm, v(55.36, -37.36) * mm]});
            skFitSpline(sketch, "E252", {"points": [v(55.36, -37.36) * mm, v(56.73, -38.5) * mm, v(58.04, -38.58) * mm, v(59.47, -37.43) * mm]});
            skFitSpline(sketch, "E253", {"points": [v(59.47, -37.43) * mm, v(61.96, -35.42) * mm, v(62.91, -32.72) * mm, v(62.46, -29.64) * mm]});
            skFitSpline(sketch, "E254", {"points": [v(62.46, -29.64) * mm, v(62.01, -26.55) * mm, v(59.98, -24.52) * mm, v(57.28, -23.19) * mm]});
            skFitSpline(sketch, "E255", {"points": [v(57.28, -23.19) * mm, v(55.27, -22.2) * mm, v(53.18, -21.72) * mm, v(51.06, -21.7) * mm]});
            skFitSpline(sketch, "E256", {"points": [v(183.5, -46.44) * mm, v(182.36, -46.48) * mm, v(181.23, -46.67) * mm, v(180.11, -47.02) * mm]});
            skFitSpline(sketch, "E257", {"points": [v(180.11, -47.02) * mm, v(176.6, -48.1) * mm, v(173.82, -50.2) * mm, v(171.64, -53.12) * mm]});
            skFitSpline(sketch, "E258", {"points": [v(171.64, -53.12) * mm, v(168.61, -57.16) * mm, v(166.87, -61.61) * mm, v(167.41, -66.76) * mm]});
            skFitSpline(sketch, "E259", {"points": [v(167.41, -66.76) * mm, v(167.74, -69.88) * mm, v(169.16, -72.36) * mm, v(172.12, -73.6) * mm]});
            skFitSpline(sketch, "E260", {"points": [v(172.12, -73.6) * mm, v(173.5, -74.19) * mm, v(175.07, -74.33) * mm, v(176.44, -74.64) * mm]});
            skFitSpline(sketch, "E261", {"points": [v(176.44, -74.64) * mm, v(177.93, -74.36) * mm, v(179.27, -74.22) * mm, v(180.55, -73.86) * mm]});
            skFitSpline(sketch, "E262", {"points": [v(180.55, -73.86) * mm, v(183.84, -72.94) * mm, v(186.45, -70.94) * mm, v(188.58, -68.32) * mm]});
            skFitSpline(sketch, "E263", {"points": [v(188.58, -68.32) * mm, v(191.69, -64.5) * mm, v(193.53, -60.15) * mm, v(193.35, -55.13) * mm]});
            skFitSpline(sketch, "E264", {"points": [v(193.35, -55.13) * mm, v(193.2, -50.9) * mm, v(190.72, -47.73) * mm, v(186.92, -46.8) * mm]});
            skFitSpline(sketch, "E265", {"points": [v(186.92, -46.8) * mm, v(185.77, -46.52) * mm, v(184.63, -46.4) * mm, v(183.5, -46.44) * mm]});
            skFitSpline(sketch, "E266", {"points": [v(183.91, -47) * mm, v(184.1, -47) * mm, v(184.27, -47.02) * mm, v(184.46, -47.04) * mm]});
            skFitSpline(sketch, "E267", {"points": [v(184.46, -47.04) * mm, v(186.31, -47.26) * mm, v(187.72, -48.5) * mm, v(188.13, -50.37) * mm]});
            skFitSpline(sketch, "E268", {"points": [v(188.13, -50.37) * mm, v(188.4, -51.57) * mm, v(188.5, -52.82) * mm, v(188.62, -53.7) * mm]});
            skFitSpline(sketch, "E269", {"points": [v(188.62, -53.7) * mm, v(188.23, -60.31) * mm, v(186.23, -65.94) * mm, v(182.23, -70.78) * mm]});
            skFitSpline(sketch, "E270", {"points": [v(182.23, -70.78) * mm, v(181.04, -72.23) * mm, v(179.54, -73.36) * mm, v(177.64, -73.82) * mm]});
            skFitSpline(sketch, "E271", {"points": [v(177.64, -73.82) * mm, v(175.61, -74.3) * mm, v(173.77, -73.4) * mm, v(173, -71.45) * mm]});
            skFitSpline(sketch, "E272", {"points": [v(173, -71.45) * mm, v(172.06, -69.15) * mm, v(172.19, -66.75) * mm, v(172.56, -64.38) * mm]});
            skFitSpline(sketch, "E273", {"points": [v(172.56, -64.38) * mm, v(173.3, -59.74) * mm, v(174.85, -55.4) * mm, v(177.59, -51.54) * mm]});
            skFitSpline(sketch, "E274", {"points": [v(177.59, -51.54) * mm, v(178.43, -50.35) * mm, v(179.5, -49.29) * mm, v(180.61, -48.32) * mm]});
            skFitSpline(sketch, "E275", {"points": [v(180.61, -48.32) * mm, v(181.54, -47.5) * mm, v(182.67, -47) * mm, v(183.91, -47) * mm]});
            skFitSpline(sketch, "E276", {"points": [v(162.59, -28.08) * mm, v(160.74, -28.07) * mm, v(159.08, -29.73) * mm, v(159.13, -31.54) * mm]});
            skFitSpline(sketch, "E277", {"points": [v(159.13, -31.54) * mm, v(159.17, -32.93) * mm, v(160.32, -34.02) * mm, v(161.76, -34.02) * mm]});
            skFitSpline(sketch, "E278", {"points": [v(161.76, -34.02) * mm, v(163.53, -34.03) * mm, v(165.1, -32.41) * mm, v(165.08, -30.6) * mm]});
            skFitSpline(sketch, "E279", {"points": [v(165.08, -30.6) * mm, v(165.07, -29.09) * mm, v(164.09, -28.09) * mm, v(162.59, -28.08) * mm]});
            skFitSpline(sketch, "E280", {"points": [v(-63.05, -34.75) * mm, v(-63.5, -34.75) * mm, v(-63.9, -34.86) * mm, v(-64.12, -35.59) * mm]});
            skLineSegment(sketch, "E281", {"start": v(-64.12, -35.59) * mm, "end": v(-56.18, -35.59) * mm});
            skFitSpline(sketch, "E282", {"points": [v(-56.18, -35.59) * mm, v(-57.53, -36.72) * mm, v(-58.06, -38.04) * mm, v(-58.46, -39.41) * mm]});
            skFitSpline(sketch, "E283", {"points": [v(-58.46, -39.41) * mm, v(-59.73, -43.82) * mm, v(-60.96, -48.24) * mm, v(-62.22, -52.65) * mm]});
            skFitSpline(sketch, "E284", {"points": [v(-62.22, -52.65) * mm, v(-62.28, -52.88) * mm, v(-62.4, -53.08) * mm, v(-62.5, -53.3) * mm]});
            skFitSpline(sketch, "E285", {"points": [v(-62.5, -53.3) * mm, v(-62.69, -52.92) * mm, v(-62.66, -52.58) * mm, v(-62.73, -52.26) * mm]});
            skFitSpline(sketch, "E286", {"points": [v(-62.73, -52.26) * mm, v(-63.38, -49.34) * mm, v(-64.83, -47.67) * mm, v(-67.71, -47.67) * mm]});
            skFitSpline(sketch, "E287", {"points": [v(-67.71, -47.67) * mm, v(-69.7, -47.66) * mm, v(-71.59, -48.14) * mm, v(-73.36, -49.08) * mm]});
            skFitSpline(sketch, "E288", {"points": [v(-73.36, -49.08) * mm, v(-77.7, -51.4) * mm, v(-80.53, -55.04) * mm, v(-82.61, -59.35) * mm]});
            skFitSpline(sketch, "E289", {"points": [v(-82.61, -59.35) * mm, v(-83.94, -62.1) * mm, v(-84.7, -65) * mm, v(-84.56, -68.08) * mm]});
            skFitSpline(sketch, "E290", {"points": [v(-84.56, -68.08) * mm, v(-84.37, -72.68) * mm, v(-81.3, -75.65) * mm, v(-76.72, -75.7) * mm]});
            skFitSpline(sketch, "E291", {"points": [v(-76.72, -75.7) * mm, v(-75.7, -75.72) * mm, v(-74.74, -75.56) * mm, v(-73.8, -75.13) * mm]});
            skFitSpline(sketch, "E292", {"points": [v(-73.8, -75.13) * mm, v(-71.8, -74.2) * mm, v(-70.19, -72.8) * mm, v(-68.8, -71.13) * mm]});
            skFitSpline(sketch, "E293", {"points": [v(-68.8, -71.13) * mm, v(-68.17, -70.37) * mm, v(-67.6, -69.57) * mm, v(-66.83, -68.57) * mm]});
            skFitSpline(sketch, "E294", {"points": [v(-66.83, -68.57) * mm, v(-66.83, -69.27) * mm, v(-66.83, -69.73) * mm, v(-66.83, -70.19) * mm]});
            skFitSpline(sketch, "E295", {"points": [v(-66.83, -70.19) * mm, v(-66.83, -72.46) * mm, v(-65.7, -73.97) * mm, v(-63.7, -74.89) * mm]});
            skFitSpline(sketch, "E296", {"points": [v(-63.7, -74.89) * mm, v(-63.26, -75.09) * mm, v(-62.8, -75.27) * mm, v(-62.35, -75.4) * mm]});
            skFitSpline(sketch, "E297", {"points": [v(-62.35, -75.4) * mm, v(-60.75, -75.86) * mm, v(-59.27, -75.82) * mm, v(-57.92, -75.31) * mm]});
            skFitSpline(sketch, "E298", {"points": [v(-57.23, -75.03) * mm, v(-55.23, -74.09) * mm, v(-54.05, -72.26) * mm, v(-53.25, -70.13) * mm]});
            skFitSpline(sketch, "E299", {"points": [v(-53.25, -70.13) * mm, v(-52.97, -69.4) * mm, v(-52.88, -68.61) * mm, v(-52.64, -67.58) * mm]});
            skFitSpline(sketch, "E300", {"points": [v(-52.64, -67.58) * mm, v(-53.49, -68.31) * mm, v(-53.43, -68.33) * mm, v(-53.63, -69.06) * mm]});
            skFitSpline(sketch, "E301", {"points": [v(-53.63, -69.06) * mm, v(-54.29, -71.44) * mm, v(-55.4, -73.43) * mm, v(-57.63, -74.47) * mm]});
            skFitSpline(sketch, "E302", {"points": [v(-58.29, -74.77) * mm, v(-60.38, -75.6) * mm, v(-61.9, -74.7) * mm, v(-61.87, -72.47) * mm]});
            skFitSpline(sketch, "E303", {"points": [v(-61.87, -72.47) * mm, v(-61.86, -71.34) * mm, v(-61.7, -70.18) * mm, v(-61.4, -69.08) * mm]});
            skFitSpline(sketch, "E304", {"points": [v(-61.4, -69.08) * mm, v(-60.58, -65.99) * mm, v(-59.64, -62.92) * mm, v(-58.78, -59.84) * mm]});
            skFitSpline(sketch, "E305", {"points": [v(-58.78, -59.84) * mm, v(-56.92, -53.16) * mm, v(-55.07, -46.48) * mm, v(-53.22, -39.8) * mm]});
            skFitSpline(sketch, "E306", {"points": [v(-53.22, -39.8) * mm, v(-52.8, -38.26) * mm, v(-51.94, -34.88) * mm, v(-51.81, -34.75) * mm]});
            skFitSpline(sketch, "E307", {"points": [v(-51.81, -34.75) * mm, v(-52.95, -34.75) * mm, v(-61.91, -34.76) * mm, v(-63.05, -34.75) * mm]});
            skFitSpline(sketch, "E308", {"points": [v(-67.5, -48.36) * mm, v(-66.33, -48.4) * mm, v(-65.23, -48.87) * mm, v(-64.46, -49.76) * mm]});
            skFitSpline(sketch, "E309", {"points": [v(-64.46, -49.76) * mm, v(-63.71, -50.62) * mm, v(-63.45, -51.69) * mm, v(-63.34, -52.79) * mm]});
            skFitSpline(sketch, "E310", {"points": [v(-63.34, -52.79) * mm, v(-63.29, -53.36) * mm, v(-63.33, -53.94) * mm, v(-63.33, -54.51) * mm]});
            skFitSpline(sketch, "E311", {"points": [v(-63.33, -54.51) * mm, v(-63.25, -54.52) * mm, v(-63.18, -54.54) * mm, v(-63.1, -54.55) * mm]});
            skFitSpline(sketch, "E312", {"points": [v(-63.1, -54.55) * mm, v(-63.37, -55.94) * mm, v(-63.55, -57.36) * mm, v(-63.94, -58.72) * mm]});
            skFitSpline(sketch, "E313", {"points": [v(-63.94, -58.72) * mm, v(-64.64, -61.15) * mm, v(-65.26, -63.63) * mm, v(-66.29, -65.92) * mm]});
            skFitSpline(sketch, "E314", {"points": [v(-66.29, -65.92) * mm, v(-67.92, -69.56) * mm, v(-70.37, -72.59) * mm, v(-74.03, -74.44) * mm]});
            skFitSpline(sketch, "E315", {"points": [v(-74.03, -74.44) * mm, v(-74.37, -74.62) * mm, v(-74.73, -74.76) * mm, v(-75.1, -74.87) * mm]});
            skFitSpline(sketch, "E316", {"points": [v(-75.1, -74.87) * mm, v(-76.84, -75.4) * mm, v(-78.48, -74.6) * mm, v(-79.15, -72.9) * mm]});
            skFitSpline(sketch, "E317", {"points": [v(-79.15, -72.9) * mm, v(-79.92, -70.95) * mm, v(-79.83, -68.92) * mm, v(-79.52, -66.95) * mm]});
            skFitSpline(sketch, "E318", {"points": [v(-79.52, -66.95) * mm, v(-78.77, -62.14) * mm, v(-77.07, -57.64) * mm, v(-74.45, -53.5) * mm]});
            skFitSpline(sketch, "E319", {"points": [v(-74.45, -53.5) * mm, v(-73.5, -52) * mm, v(-72.31, -50.7) * mm, v(-70.94, -49.57) * mm]});
            skFitSpline(sketch, "E320", {"points": [v(-70.94, -49.57) * mm, v(-69.9, -48.73) * mm, v(-68.67, -48.33) * mm, v(-67.5, -48.36) * mm]});
            skFitSpline(sketch, "E321", {"points": [v(-31.94, -47.69) * mm, v(-32.9, -47.67) * mm, v(-33.85, -47.79) * mm, v(-34.8, -48.02) * mm]});
            skFitSpline(sketch, "E322", {"points": [v(-34.8, -48.02) * mm, v(-37.93, -48.78) * mm, v(-40.43, -50.61) * mm, v(-42.59, -52.9) * mm]});
            skFitSpline(sketch, "E323", {"points": [v(-42.59, -52.9) * mm, v(-44.47, -54.88) * mm, v(-45.99, -57.16) * mm, v(-47.08, -59.68) * mm]});
            skFitSpline(sketch, "E324", {"points": [v(-47.08, -59.68) * mm, v(-48.27, -62.42) * mm, v(-49.14, -65.25) * mm, v(-48.96, -68.3) * mm]});
            skFitSpline(sketch, "E325", {"points": [v(-48.96, -68.3) * mm, v(-48.7, -72.6) * mm, v(-45.96, -75.45) * mm, v(-41.4, -75.7) * mm]});
            skFitSpline(sketch, "E326", {"points": [v(-41.4, -75.7) * mm, v(-39.07, -75.83) * mm, v(-37.2, -74.84) * mm, v(-35.6, -73.36) * mm]});
            skFitSpline(sketch, "E327", {"points": [v(-35.6, -73.36) * mm, v(-34.3, -72.17) * mm, v(-33.24, -70.74) * mm, v(-32.08, -69.42) * mm]});
            skFitSpline(sketch, "E328", {"points": [v(-32.08, -69.42) * mm, v(-31.81, -69.11) * mm, v(-31.56, -68.8) * mm, v(-31.19, -68.37) * mm]});
            skFitSpline(sketch, "E329", {"points": [v(-31.19, -68.37) * mm, v(-31.19, -69.15) * mm, v(-31.23, -69.72) * mm, v(-31.18, -70.29) * mm]});
            skFitSpline(sketch, "E330", {"points": [v(-31.18, -70.29) * mm, v(-31.07, -71.77) * mm, v(-30.57, -73.1) * mm, v(-29.4, -74.08) * mm]});
            skFitSpline(sketch, "E331", {"points": [v(-29.4, -74.08) * mm, v(-27.23, -75.91) * mm, v(-22.95, -76.58) * mm, v(-20.32, -74.05) * mm]});
            skFitSpline(sketch, "E332", {"points": [v(-20.32, -74.05) * mm, v(-20.32, -74.04) * mm, v(-20.31, -74.04) * mm, v(-20.3, -74.03) * mm]});
            skFitSpline(sketch, "E333", {"points": [v(-20.3, -74.03) * mm, v(-19.19, -73.02) * mm, v(-18.43, -71.64) * mm, v(-17.86, -70.12) * mm]});
            skFitSpline(sketch, "E334", {"points": [v(-17.86, -70.12) * mm, v(-17.6, -69.4) * mm, v(-17.5, -68.6) * mm, v(-17.26, -67.56) * mm]});
            skFitSpline(sketch, "E335", {"points": [v(-17.26, -67.56) * mm, v(-18.1, -68.3) * mm, v(-18.05, -68.32) * mm, v(-18.25, -69.05) * mm]});
            skFitSpline(sketch, "E336", {"points": [v(-18.25, -69.05) * mm, v(-18.73, -70.82) * mm, v(-19.46, -72.37) * mm, v(-20.7, -73.48) * mm]});
            skFitSpline(sketch, "E337", {"points": [v(-20.7, -73.48) * mm, v(-21, -73.74) * mm, v(-21.33, -73.99) * mm, v(-21.68, -74.2) * mm]});
            skFitSpline(sketch, "E338", {"points": [v(-21.68, -74.2) * mm, v(-21.68, -74.2) * mm, v(-21.7, -74.2) * mm, v(-21.7, -74.2) * mm]});
            skFitSpline(sketch, "E339", {"points": [v(-21.7, -74.2) * mm, v(-22.1, -74.44) * mm, v(-22.54, -74.65) * mm, v(-23.02, -74.8) * mm]});
            skFitSpline(sketch, "E340", {"points": [v(-23.02, -74.8) * mm, v(-25.18, -75.55) * mm, v(-26.56, -74.64) * mm, v(-26.44, -72.33) * mm]});
            skFitSpline(sketch, "E341", {"points": [v(-26.44, -72.33) * mm, v(-26.38, -71.11) * mm, v(-26.04, -69.9) * mm, v(-25.7, -68.7) * mm]});
            skFitSpline(sketch, "E342", {"points": [v(-25.7, -68.7) * mm, v(-23.9, -62.16) * mm, v(-20.11, -48.47) * mm, v(-20.03, -47.95) * mm]});
            skFitSpline(sketch, "E343", {"points": [v(-20.03, -47.95) * mm, v(-21.78, -47.8) * mm, v(-23.42, -47.83) * mm, v(-24.98, -47.92) * mm]});
            skFitSpline(sketch, "E344", {"points": [v(-24.98, -47.92) * mm, v(-25.17, -48.15) * mm, v(-26.3, -51.45) * mm, v(-26.8, -53.02) * mm]});
            skFitSpline(sketch, "E345", {"points": [v(-26.8, -53.02) * mm, v(-27.21, -51.87) * mm, v(-27.5, -50.76) * mm, v(-28.01, -49.77) * mm]});
            skFitSpline(sketch, "E346", {"points": [v(-28.01, -49.77) * mm, v(-28.6, -48.62) * mm, v(-29.61, -47.93) * mm, v(-30.97, -47.76) * mm]});
            skFitSpline(sketch, "E347", {"points": [v(-30.97, -47.76) * mm, v(-31.3, -47.72) * mm, v(-31.62, -47.7) * mm, v(-31.94, -47.69) * mm]});
            skFitSpline(sketch, "E348", {"points": [v(-31.99, -48.4) * mm, v(-29.92, -48.38) * mm, v(-28.63, -49.27) * mm, v(-28.07, -51.26) * mm]});
            skFitSpline(sketch, "E349", {"points": [v(-28.07, -51.26) * mm, v(-27.44, -53.52) * mm, v(-27.55, -55.8) * mm, v(-28.19, -58.05) * mm]});
            skFitSpline(sketch, "E350", {"points": [v(-28.19, -58.05) * mm, v(-28.8, -60.2) * mm, v(-29.4, -62.37) * mm, v(-30.14, -64.49) * mm]});
            skFitSpline(sketch, "E351", {"points": [v(-30.14, -64.49) * mm, v(-31.3, -67.75) * mm, v(-33.25, -70.51) * mm, v(-35.91, -72.72) * mm]});
            skFitSpline(sketch, "E352", {"points": [v(-35.91, -72.72) * mm, v(-36.85, -73.5) * mm, v(-37.98, -74.05) * mm, v(-39.05, -74.67) * mm]});
            skFitSpline(sketch, "E353", {"points": [v(-39.05, -74.67) * mm, v(-40.91, -75.73) * mm, v(-43.53, -74.83) * mm, v(-44, -71.69) * mm]});
            skFitSpline(sketch, "E354", {"points": [v(-44, -71.69) * mm, v(-44.11, -70.94) * mm, v(-44.02, -70.16) * mm, v(-44.02, -69.4) * mm]});
            skFitSpline(sketch, "E355", {"points": [v(-44.02, -69.4) * mm, v(-44.22, -66.32) * mm, v(-43.27, -63.44) * mm, v(-42.27, -60.61) * mm]});
            skFitSpline(sketch, "E356", {"points": [v(-42.27, -60.61) * mm, v(-41.01, -57.03) * mm, v(-39.3, -53.66) * mm, v(-36.67, -50.87) * mm]});
            skFitSpline(sketch, "E357", {"points": [v(-36.67, -50.87) * mm, v(-35.4, -49.54) * mm, v(-33.98, -48.42) * mm, v(-31.99, -48.4) * mm]});
            skFitSpline(sketch, "E358", {"points": [v(75.28, -36.95) * mm, v(74.54, -37.91) * mm, v(74.05, -38.75) * mm, v(73.38, -39.4) * mm]});
            skFitSpline(sketch, "E359", {"points": [v(73.38, -39.4) * mm, v(72.7, -40.05) * mm, v(71.85, -40.54) * mm, v(71.07, -41.09) * mm]});
            skFitSpline(sketch, "E360", {"points": [v(71.07, -41.09) * mm, v(69.62, -42.1) * mm, v(68.48, -43.34) * mm, v(67.9, -45.05) * mm]});
            skFitSpline(sketch, "E361", {"points": [v(67.9, -45.05) * mm, v(67.7, -45.67) * mm, v(67.41, -46.26) * mm, v(67.16, -46.87) * mm]});
            skFitSpline(sketch, "E362", {"points": [v(67.16, -46.87) * mm, v(65.97, -46.87) * mm, v(65.04, -46.87) * mm, v(64.72, -46.87) * mm]});
            skFitSpline(sketch, "E363", {"points": [v(64.72, -46.87) * mm, v(64.28, -46.87) * mm, v(63.88, -46.98) * mm, v(63.65, -47.7) * mm]});
            skFitSpline(sketch, "E364", {"points": [v(63.65, -47.7) * mm, v(64.7, -47.7) * mm, v(66.82, -47.73) * mm, v(66.93, -47.75) * mm]});
            skFitSpline(sketch, "E365", {"points": [v(66.93, -47.75) * mm, v(66.84, -48.2) * mm, v(66.8, -48.56) * mm, v(66.69, -48.92) * mm]});
            skFitSpline(sketch, "E366", {"points": [v(66.69, -48.92) * mm, v(65.5, -53.05) * mm, v(64.3, -57.19) * mm, v(63.13, -61.32) * mm]});
            skFitSpline(sketch, "E367", {"points": [v(63.13, -61.32) * mm, v(62.53, -63.44) * mm, v(61.9, -65.54) * mm, v(61.38, -67.68) * mm]});
            skFitSpline(sketch, "E368", {"points": [v(61.38, -67.68) * mm, v(60.8, -70.09) * mm, v(61.6, -72.17) * mm, v(63.71, -73.33) * mm]});
            skFitSpline(sketch, "E369", {"points": [v(63.71, -73.33) * mm, v(67.63, -75.48) * mm, v(71.68, -74.62) * mm, v(73.8, -70.9) * mm]});
            skFitSpline(sketch, "E370", {"points": [v(74.9, -67.63) * mm, v(74.18, -68.24) * mm, v(74.23, -68.25) * mm, v(74.05, -68.86) * mm]});
            skFitSpline(sketch, "E371", {"points": [v(74.05, -68.86) * mm, v(73.85, -69.52) * mm, v(73.6, -70.13) * mm, v(73.31, -70.7) * mm]});
            skFitSpline(sketch, "E372", {"points": [v(73.31, -70.7) * mm, v(72.33, -72.24) * mm, v(70.98, -73.4) * mm, v(68.98, -73.88) * mm]});
            skFitSpline(sketch, "E373", {"points": [v(68.98, -73.88) * mm, v(67.3, -74.27) * mm, v(66.07, -73.41) * mm, v(66.05, -71.69) * mm]});
            skFitSpline(sketch, "E374", {"points": [v(66.05, -71.69) * mm, v(66.04, -70.56) * mm, v(66.2, -69.39) * mm, v(66.5, -68.3) * mm]});
            skFitSpline(sketch, "E375", {"points": [v(66.5, -68.3) * mm, v(68.08, -62.63) * mm, v(69.73, -57) * mm, v(71.36, -51.35) * mm]});
            skFitSpline(sketch, "E376", {"points": [v(71.36, -51.35) * mm, v(71.7, -50.15) * mm, v(72.1, -48.97) * mm, v(72.5, -47.7) * mm]});
            skLineSegment(sketch, "E377", {"start": v(72.5, -47.7) * mm, "end": v(78.61, -47.7) * mm});
            skFitSpline(sketch, "E378", {"points": [v(78.61, -47.7) * mm, v(78.89, -47.43) * mm, v(78.86, -47.16) * mm, v(79.14, -46.9) * mm]});
            skFitSpline(sketch, "E379", {"points": [v(79.14, -46.9) * mm, v(78.5, -46.89) * mm, v(75.47, -46.88) * mm, v(72.67, -46.87) * mm]});
            skFitSpline(sketch, "E380", {"points": [v(72.67, -46.87) * mm, v(72.97, -45.87) * mm, v(73.2, -45.1) * mm, v(73.42, -44.31) * mm]});
            skFitSpline(sketch, "E381", {"points": [v(73.42, -44.31) * mm, v(73.65, -43.53) * mm, v(73.86, -42.74) * mm, v(74.08, -41.96) * mm]});
            skFitSpline(sketch, "E382", {"points": [v(74.08, -41.96) * mm, v(74.32, -41.14) * mm, v(74.59, -40.32) * mm, v(74.8, -39.48) * mm]});
            skFitSpline(sketch, "E383", {"points": [v(74.8, -39.48) * mm, v(74.98, -38.72) * mm, v(75.41, -37.98) * mm, v(75.28, -36.95) * mm]});
            skFitSpline(sketch, "E384", {"points": [v(82.6, -46.87) * mm, v(82.17, -46.87) * mm, v(81.76, -46.98) * mm, v(81.54, -47.7) * mm]});
            skLineSegment(sketch, "E385", {"start": v(81.54, -47.7) * mm, "end": v(87.69, -47.7) * mm});
            skFitSpline(sketch, "E386", {"points": [v(87.69, -47.7) * mm, v(86.07, -48.66) * mm, v(84.96, -49.93) * mm, v(84.45, -51.66) * mm]});
            skFitSpline(sketch, "E387", {"points": [v(84.45, -51.66) * mm, v(82.94, -56.7) * mm, v(81.46, -61.74) * mm, v(80, -66.8) * mm]});
            skFitSpline(sketch, "E388", {"points": [v(80, -66.8) * mm, v(79.64, -68.05) * mm, v(79.6, -69.35) * mm, v(80.01, -70.62) * mm]});
            skFitSpline(sketch, "E389", {"points": [v(80.01, -70.62) * mm, v(80.95, -73.54) * mm, v(84.26, -75.14) * mm, v(87.49, -74.3) * mm]});
            skFitSpline(sketch, "E390", {"points": [v(87.49, -74.3) * mm, v(90.26, -73.58) * mm, v(92.29, -71.8) * mm, v(94.07, -69.68) * mm]});
            skFitSpline(sketch, "E391", {"points": [v(94.07, -69.68) * mm, v(94.77, -68.85) * mm, v(95.4, -67.97) * mm, v(96.26, -66.83) * mm]});
            skFitSpline(sketch, "E392", {"points": [v(96.26, -66.83) * mm, v(96.14, -67.54) * mm, v(96.08, -67.9) * mm, v(96.03, -68.27) * mm]});
            skFitSpline(sketch, "E393", {"points": [v(96.03, -68.27) * mm, v(95.81, -69.88) * mm, v(96.18, -71.32) * mm, v(97.33, -72.5) * mm]});
            skFitSpline(sketch, "E394", {"points": [v(97.33, -72.5) * mm, v(100.24, -75.54) * mm, v(105.63, -75.15) * mm, v(108.08, -71.75) * mm]});
            skFitSpline(sketch, "E395", {"points": [v(108.08, -71.75) * mm, v(108.48, -71.2) * mm, v(108.78, -70.6) * mm, v(109.08, -70.01) * mm]});
            skFitSpline(sketch, "E396", {"points": [v(109.74, -67.57) * mm, v(108.95, -68.23) * mm, v(108.95, -68.23) * mm, v(108.8, -68.9) * mm]});
            skFitSpline(sketch, "E397", {"points": [v(108.8, -68.9) * mm, v(108.65, -69.63) * mm, v(108.41, -70.05) * mm, v(108.16, -70.58) * mm]});
            skFitSpline(sketch, "E398", {"points": [v(108.16, -70.58) * mm, v(107.81, -71.15) * mm, v(107.42, -71.7) * mm, v(106.94, -72.18) * mm]});
            skFitSpline(sketch, "E399", {"points": [v(106.94, -72.18) * mm, v(105.92, -73.23) * mm, v(104.71, -74) * mm, v(103.17, -74) * mm]});
            skFitSpline(sketch, "E400", {"points": [v(103.17, -74) * mm, v(101.76, -74.01) * mm, v(100.97, -73.4) * mm, v(100.87, -72.01) * mm]});
            skFitSpline(sketch, "E401", {"points": [v(100.87, -72.01) * mm, v(100.8, -71.12) * mm, v(100.83, -70.17) * mm, v(101.06, -69.31) * mm]});
            skFitSpline(sketch, "E402", {"points": [v(101.06, -69.31) * mm, v(102.67, -63.5) * mm, v(104.34, -57.72) * mm, v(105.98, -51.93) * mm]});
            skFitSpline(sketch, "E403", {"points": [v(105.98, -51.93) * mm, v(106.42, -50.38) * mm, v(106.85, -48.83) * mm, v(107.35, -47.06) * mm]});
            skFitSpline(sketch, "E404", {"points": [v(107.35, -47.06) * mm, v(105.47, -46.93) * mm, v(103.83, -46.92) * mm, v(102.2, -47.07) * mm]});
            skFitSpline(sketch, "E405", {"points": [v(102.2, -47.07) * mm, v(102.02, -47.48) * mm, v(99.55, -55.7) * mm, v(98.49, -59.53) * mm]});
            skFitSpline(sketch, "E406", {"points": [v(98.49, -59.53) * mm, v(97.2, -64.2) * mm, v(95.08, -68.35) * mm, v(91.4, -71.6) * mm]});
            skFitSpline(sketch, "E407", {"points": [v(91.4, -71.6) * mm, v(90.16, -72.7) * mm, v(88.74, -73.5) * mm, v(87.13, -73.86) * mm]});
            skFitSpline(sketch, "E408", {"points": [v(87.13, -73.86) * mm, v(86.03, -74.12) * mm, v(84.83, -74.35) * mm, v(83.87, -72.95) * mm]});
            skFitSpline(sketch, "E409", {"points": [v(83.87, -72.95) * mm, v(83.7, -72.4) * mm, v(83.93, -71.61) * mm, v(84.14, -70.9) * mm]});
            skFitSpline(sketch, "E410", {"points": [v(84.14, -70.9) * mm, v(86.26, -63.5) * mm, v(90.92, -46.94) * mm, v(90.97, -46.87) * mm]});
            skFitSpline(sketch, "E411", {"points": [v(90.97, -46.87) * mm, v(89.13, -46.87) * mm, v(83.04, -46.87) * mm, v(82.6, -46.87) * mm]});
            skFitSpline(sketch, "E412", {"points": [v(134.74, -33.6) * mm, v(134.3, -33.6) * mm, v(133.9, -33.72) * mm, v(133.67, -34.44) * mm]});
            skLineSegment(sketch, "E413", {"start": v(133.67, -34.44) * mm, "end": v(141.53, -34.44) * mm});
            skFitSpline(sketch, "E414", {"points": [v(141.53, -34.44) * mm, v(140.08, -35.76) * mm, v(139.5, -37.26) * mm, v(139.07, -38.8) * mm]});
            skFitSpline(sketch, "E415", {"points": [v(139.07, -38.8) * mm, v(137.98, -42.63) * mm, v(136.92, -46.45) * mm, v(135.85, -50.27) * mm]});
            skFitSpline(sketch, "E416", {"points": [v(135.85, -50.27) * mm, v(135.63, -51.02) * mm, v(135.4, -51.77) * mm, v(135.16, -52.52) * mm]});
            skFitSpline(sketch, "E417", {"points": [v(135.16, -52.52) * mm, v(134.86, -52.1) * mm, v(134.85, -51.74) * mm, v(134.81, -51.38) * mm]});
            skFitSpline(sketch, "E418", {"points": [v(134.81, -51.38) * mm, v(134.51, -48.42) * mm, v(132.62, -46.72) * mm, v(129.69, -46.7) * mm]});
            skFitSpline(sketch, "E419", {"points": [v(129.69, -46.7) * mm, v(126.44, -46.68) * mm, v(123.74, -48.04) * mm, v(121.33, -50.04) * mm]});
            skFitSpline(sketch, "E420", {"points": [v(121.33, -50.04) * mm, v(117.46, -53.25) * mm, v(115, -57.4) * mm, v(113.63, -62.22) * mm]});
            skFitSpline(sketch, "E421", {"points": [v(113.63, -62.22) * mm, v(113.08, -64.14) * mm, v(113, -66.1) * mm, v(113.23, -68.06) * mm]});
            skFitSpline(sketch, "E422", {"points": [v(113.23, -68.06) * mm, v(113.41, -69.7) * mm, v(114.08, -71.2) * mm, v(115.28, -72.39) * mm]});
            skFitSpline(sketch, "E423", {"points": [v(115.28, -72.39) * mm, v(117.7, -74.8) * mm, v(121.88, -75.27) * mm, v(124.85, -73.47) * mm]});
            skFitSpline(sketch, "E424", {"points": [v(124.85, -73.47) * mm, v(126.93, -72.2) * mm, v(128.55, -70.46) * mm, v(129.94, -68.49) * mm]});
            skFitSpline(sketch, "E425", {"points": [v(129.94, -68.49) * mm, v(130.17, -68.17) * mm, v(130.43, -67.88) * mm, v(130.67, -67.58) * mm]});
            skFitSpline(sketch, "E426", {"points": [v(130.67, -67.58) * mm, v(130.84, -68.03) * mm, v(130.8, -68.35) * mm, v(130.8, -68.68) * mm]});
            skFitSpline(sketch, "E427", {"points": [v(130.8, -68.68) * mm, v(130.71, -70.53) * mm, v(131.38, -72.07) * mm, v(132.89, -73.15) * mm]});
            skFitSpline(sketch, "E428", {"points": [v(132.89, -73.15) * mm, v(134.88, -74.58) * mm, v(137.16, -74.91) * mm, v(139.46, -74.26) * mm]});
            skFitSpline(sketch, "E429", {"points": [v(139.46, -74.26) * mm, v(141.48, -73.69) * mm, v(143.3, -71.63) * mm, v(144.12, -69.34) * mm]});
            skFitSpline(sketch, "E430", {"points": [v(143.82, -68.6) * mm, v(143.42, -69.81) * mm, v(142.85, -70.95) * mm, v(141.98, -71.92) * mm]});
            skFitSpline(sketch, "E431", {"points": [v(141.98, -71.92) * mm, v(140.86, -73.17) * mm, v(139.53, -74.07) * mm, v(137.76, -74) * mm]});
            skFitSpline(sketch, "E432", {"points": [v(137.76, -74) * mm, v(136.65, -73.96) * mm, v(136.02, -73.54) * mm, v(135.81, -72.46) * mm]});
            skFitSpline(sketch, "E433", {"points": [v(135.81, -72.46) * mm, v(135.65, -71.58) * mm, v(135.59, -70.62) * mm, v(135.79, -69.77) * mm]});
            skFitSpline(sketch, "E434", {"points": [v(135.79, -69.77) * mm, v(136.5, -66.74) * mm, v(137.33, -63.75) * mm, v(138.16, -60.76) * mm]});
            skFitSpline(sketch, "E435", {"points": [v(138.16, -60.76) * mm, v(139.99, -54.17) * mm, v(145.8, -33.9) * mm, v(146.08, -33.63) * mm]});
            skFitSpline(sketch, "E436", {"points": [v(146.08, -33.63) * mm, v(144.94, -33.62) * mm, v(135.88, -33.61) * mm, v(134.74, -33.6) * mm]});
            skFitSpline(sketch, "E437", {"points": [v(130.17, -47.28) * mm, v(132.5, -47.26) * mm, v(133.88, -48.71) * mm, v(134.38, -51.6) * mm]});
            skFitSpline(sketch, "E438", {"points": [v(134.38, -51.6) * mm, v(134.48, -52.21) * mm, v(134.4, -52.85) * mm, v(134.4, -53.47) * mm]});
            skFitSpline(sketch, "E439", {"points": [v(134.4, -53.47) * mm, v(134.56, -56.27) * mm, v(133.3, -58.76) * mm, v(132.67, -61.4) * mm]});
            skFitSpline(sketch, "E440", {"points": [v(132.67, -61.4) * mm, v(131.82, -64.94) * mm, v(130, -67.92) * mm, v(127.52, -70.53) * mm]});
            skFitSpline(sketch, "E441", {"points": [v(127.52, -70.53) * mm, v(126.3, -71.83) * mm, v(124.9, -72.9) * mm, v(123.26, -73.63) * mm]});
            skFitSpline(sketch, "E442", {"points": [v(123.26, -73.63) * mm, v(120.92, -74.65) * mm, v(118.96, -73.71) * mm, v(118.23, -71.26) * mm]});
            skFitSpline(sketch, "E443", {"points": [v(118.23, -71.26) * mm, v(117.66, -69.33) * mm, v(117.83, -67.35) * mm, v(118.14, -65.43) * mm]});
            skFitSpline(sketch, "E444", {"points": [v(118.14, -65.43) * mm, v(118.88, -60.8) * mm, v(120.5, -56.46) * mm, v(123.08, -52.55) * mm]});
            skFitSpline(sketch, "E445", {"points": [v(123.08, -52.55) * mm, v(124.02, -51.13) * mm, v(125.22, -49.84) * mm, v(126.47, -48.68) * mm]});
            skFitSpline(sketch, "E446", {"points": [v(126.47, -48.68) * mm, v(127.16, -48.04) * mm, v(128.18, -47.54) * mm, v(129.11, -47.38) * mm]});
            skFitSpline(sketch, "E447", {"points": [v(129.11, -47.38) * mm, v(129.49, -47.32) * mm, v(129.84, -47.28) * mm, v(130.17, -47.28) * mm]});
            skFitSpline(sketch, "E448", {"points": [v(162.9, -67.58) * mm, v(162.4, -68) * mm, v(162.29, -68.12) * mm, v(162.2, -68.4) * mm]});
            skLineSegment(sketch, "E449", {"start": v(162.2, -68.4) * mm, "end": v(162.2, -68.4) * mm});
            skFitSpline(sketch, "E450", {"points": [v(162.2, -68.4) * mm, v(161.35, -70.94) * mm, v(159.98, -73.02) * mm, v(157.18, -73.8) * mm]});
            skFitSpline(sketch, "E451", {"points": [v(157.18, -73.8) * mm, v(155.05, -74.4) * mm, v(153.86, -73.52) * mm, v(153.98, -71.32) * mm]});
            skFitSpline(sketch, "E452", {"points": [v(153.98, -71.32) * mm, v(154.05, -69.95) * mm, v(154.34, -68.57) * mm, v(154.72, -67.25) * mm]});
            skFitSpline(sketch, "E453", {"points": [v(154.72, -67.25) * mm, v(156.49, -61) * mm, v(160.42, -47.02) * mm, v(160.47, -46.97) * mm]});
            skFitSpline(sketch, "E454", {"points": [v(160.47, -46.97) * mm, v(159.33, -46.97) * mm, v(153.15, -46.95) * mm, v(152, -46.95) * mm]});
            skFitSpline(sketch, "E455", {"points": [v(152, -46.95) * mm, v(151.57, -46.95) * mm, v(151.16, -47.06) * mm, v(150.94, -47.78) * mm]});
            skLineSegment(sketch, "E456", {"start": v(150.94, -47.78) * mm, "end": v(157.17, -47.78) * mm});
            skFitSpline(sketch, "E457", {"points": [v(157.17, -47.78) * mm, v(155.03, -48.88) * mm, v(154.1, -50.8) * mm, v(153.5, -52.98) * mm]});
            skFitSpline(sketch, "E458", {"points": [v(153.5, -52.98) * mm, v(152.91, -55.05) * mm, v(152.32, -57.12) * mm, v(151.73, -59.18) * mm]});
            skFitSpline(sketch, "E459", {"points": [v(151.73, -59.18) * mm, v(150.9, -62.08) * mm, v(150, -64.96) * mm, v(149.26, -67.87) * mm]});
            skFitSpline(sketch, "E460", {"points": [v(149.26, -67.87) * mm, v(148.74, -69.9) * mm, v(149.38, -71.65) * mm, v(151.02, -73) * mm]});
            skFitSpline(sketch, "E461", {"points": [v(151.02, -73) * mm, v(153, -74.62) * mm, v(156.74, -75.02) * mm, v(158.9, -73.7) * mm]});
            skFitSpline(sketch, "E462", {"points": [v(158.9, -73.7) * mm, v(160.72, -72.56) * mm, v(161.9, -71.04) * mm, v(162.53, -69.1) * mm]});
            skLineSegment(sketch, "E463", {"start": v(-58.29, -74.77) * mm, "end": v(-57.63, -74.47) * mm});
            skLineSegment(sketch, "E464", {"start": v(-57.92, -75.31) * mm, "end": v(-57.23, -75.03) * mm});
            skLineSegment(sketch, "E465", {"start": v(73.8, -70.9) * mm, "end": v(74.95, -68.33) * mm});
            skLineSegment(sketch, "E466", {"start": v(74.95, -68.33) * mm, "end": v(74.9, -67.63) * mm});
            skLineSegment(sketch, "E467", {"start": v(109.08, -70.01) * mm, "end": v(109.45, -68.93) * mm});
            skLineSegment(sketch, "E468", {"start": v(109.45, -68.93) * mm, "end": v(109.62, -68.28) * mm});
            skLineSegment(sketch, "E469", {"start": v(109.62, -68.28) * mm, "end": v(109.74, -67.57) * mm});
            skLineSegment(sketch, "E470", {"start": v(143.82, -68.6) * mm, "end": v(143.95, -68.31) * mm});
            skLineSegment(sketch, "E471", {"start": v(143.95, -68.31) * mm, "end": v(144.08, -68.08) * mm});
            skLineSegment(sketch, "E472", {"start": v(144.08, -68.08) * mm, "end": v(144.25, -67.9) * mm});
            skLineSegment(sketch, "E473", {"start": v(144.25, -67.9) * mm, "end": v(144.55, -67.67) * mm});
            skLineSegment(sketch, "E474", {"start": v(144.12, -69.34) * mm, "end": v(144.55, -67.67) * mm});
            skLineSegment(sketch, "E475", {"start": v(162.9, -67.58) * mm, "end": v(162.53, -69.1) * mm});
            skSolve(sketch);
        }
        {
            var Q0;
            Q0 = qSketchRegion(id + "F0", true);
            extrude(context, id + "F1", {"entities" : qUnion([Q0]), "depth" : 50 * mm, "offsetDistance" : 25 * mm});
        }
        {
            var Q0;
            Q0=qCreatedBy(makeId("Front.planeOp"),FACE);
            var sketch = newSketch(context, id + "F2", { "sketchPlane" : qUnion([Q0])});
            skLineSegment(sketch, "E476.bottom", {"start": v(-300.49, 12.28) * mm, "end": v(267.43, 12.28) * mm});
            skLineSegment(sketch, "E476.top", {"start": v(-300.49, -86.25) * mm, "end": v(267.43, -86.25) * mm});
            skLineSegment(sketch, "E476.left", {"start": v(-300.49, 12.28) * mm, "end": v(-300.49, -86.25) * mm});
            skLineSegment(sketch, "E476.right", {"start": v(267.43, 12.28) * mm, "end": v(267.43, -86.25) * mm});
            skSolve(sketch);
        }
        {
            var Q0;
            Q0=makeQuery(id+"F2.imprint","IMPRINT",FACE,{"disambiguationData":[TD([[makeQuery(id+"F2.imprint","IMPRINT",EDGE,{"derivedFrom":sQuery(id+"F2.wireOp",EDGE,"E476.bottom")}),-1.0]])]});
            extrude(context, id + "F3", {"entities" : qUnion([Q0]), "depth" : 50 * mm, "offsetDistance" : 25 * mm});
        }
        {
            var Q0;
            Q0=makeQuery(id+"F3.opExtrude","CAP_FACE",FACE,{"disambiguationData":[OSD([sQuery(id+"F2.wireOp",EDGE,"E476.bottom"),sQuery(id+"F2.wireOp",EDGE,"E476.top"),sQuery(id+"F2.wireOp",EDGE,"E476.left"),sQuery(id+"F2.wireOp",EDGE,"E476.right")])],"isStart":true});
            var sketch = newSketch(context, id + "F4", { "sketchPlane" : qUnion([Q0])});
            skLineSegment(sketch, "E477.bottom", {"start": v(-208.64, -12.6) * mm, "end": v(207.27, -12.6) * mm});
            skLineSegment(sketch, "E477.top", {"start": v(-208.64, -80.86) * mm, "end": v(207.27, -80.86) * mm});
            skLineSegment(sketch, "E477.left", {"start": v(-208.64, -12.6) * mm, "end": v(-208.64, -80.86) * mm});
            skLineSegment(sketch, "E477.right", {"start": v(207.27, -12.6) * mm, "end": v(207.27, -80.86) * mm});
            skSolve(sketch);
        }
        {
            var Q0;
            Q0=makeQuery(id+"F4.imprint","IMPRINT",FACE,{"disambiguationData":[TD([[makeQuery(id+"F4.imprint","IMPRINT",EDGE,{"derivedFrom":sQuery(id+"F4.wireOp",EDGE,"E477.bottom")}),-1.0]])]});
            extrude(context, id + "F5", {"entities" : qUnion([Q0]), "oppositeDirection" : true, "depth" : 10 * mm, "offsetDistance" : 25 * mm});
        }
        {
            var Q0;
            Q0=makeQuery(id+"F5.opExtrude","CAP_FACE",FACE,{"disambiguationData":[OSD([sQuery(id+"F4.wireOp",EDGE,"E477.bottom"),sQuery(id+"F4.wireOp",EDGE,"E477.top"),sQuery(id+"F4.wireOp",EDGE,"E477.left"),sQuery(id+"F4.wireOp",EDGE,"E477.right")])],"isStart":false});
            var sketch = newSketch(context, id + "F6", { "sketchPlane" : qUnion([Q0])});
            skFitSpline(sketch, "E478", {"points": [v(-152.57, -16.96) * mm, v(-152.8, -16.97) * mm, v(-153.05, -17) * mm, v(-153.3, -17.02) * mm]});
            skFitSpline(sketch, "E479", {"points": [v(-153.3, -17.02) * mm, v(-155.95, -17.38) * mm, v(-157.67, -19.86) * mm, v(-157.09, -22.46) * mm]});
            skFitSpline(sketch, "E480", {"points": [v(-157.09, -22.46) * mm, v(-156.93, -23.15) * mm, v(-156.6, -23.68) * mm, v(-155.79, -23.95) * mm]});
            skFitSpline(sketch, "E481", {"points": [v(-155.79, -23.95) * mm, v(-155.52, -23.29) * mm, v(-155.27, -22.68) * mm, v(-155.03, -22.07) * mm]});
            skFitSpline(sketch, "E482", {"points": [v(-155.03, -22.07) * mm, v(-154.38, -20.43) * mm, v(-153.16, -19.43) * mm, v(-151.49, -19) * mm]});
            skFitSpline(sketch, "E483", {"points": [v(-151.49, -19) * mm, v(-149.95, -18.61) * mm, v(-148.22, -19.14) * mm, v(-147.38, -21.42) * mm]});
            skFitSpline(sketch, "E484", {"points": [v(-147.38, -21.42) * mm, v(-147.05, -22.57) * mm, v(-147.2, -23.02) * mm, v(-147.38, -23.59) * mm]});
            skFitSpline(sketch, "E485", {"points": [v(-147.38, -23.59) * mm, v(-148.09, -25.3) * mm, v(-149.05, -26.63) * mm, v(-150.53, -27.56) * mm]});
            skFitSpline(sketch, "E486", {"points": [v(-150.53, -27.56) * mm, v(-152.51, -28.82) * mm, v(-154.7, -29.58) * mm, v(-156.97, -29.88) * mm]});
            skFitSpline(sketch, "E487", {"points": [v(-156.97, -29.88) * mm, v(-160.51, -30.34) * mm, v(-164.1, -30.66) * mm, v(-167.67, -30.8) * mm]});
            skFitSpline(sketch, "E488", {"points": [v(-167.67, -30.8) * mm, v(-170.5, -30.9) * mm, v(-173.29, -31.24) * mm, v(-176.08, -31.61) * mm]});
            skFitSpline(sketch, "E489", {"points": [v(-176.08, -31.61) * mm, v(-185.1, -32.82) * mm, v(-192.47, -40.73) * mm, v(-193.07, -49.26) * mm]});
            skFitSpline(sketch, "E490", {"points": [v(-193.07, -49.26) * mm, v(-193.3, -52.4) * mm, v(-192.9, -55.36) * mm, v(-191.42, -58.14) * mm]});
            skFitSpline(sketch, "E491", {"points": [v(-191.42, -58.14) * mm, v(-189.28, -62.16) * mm, v(-185.83, -64.16) * mm, v(-181.36, -64.49) * mm]});
            skFitSpline(sketch, "E492", {"points": [v(-181.36, -64.49) * mm, v(-178.5, -64.7) * mm, v(-175.74, -64.23) * mm, v(-173.09, -63.1) * mm]});
            skFitSpline(sketch, "E493", {"points": [v(-173.09, -63.1) * mm, v(-168.97, -61.35) * mm, v(-165.74, -58.65) * mm, v(-163.96, -54.44) * mm]});
            skFitSpline(sketch, "E494", {"points": [v(-163.96, -54.44) * mm, v(-163.26, -52.76) * mm, v(-163.02, -51.01) * mm, v(-163.6, -49.26) * mm]});
            skFitSpline(sketch, "E495", {"points": [v(-163.6, -49.26) * mm, v(-164.22, -47.44) * mm, v(-165.81, -46.93) * mm, v(-167.64, -48.05) * mm]});
            skFitSpline(sketch, "E496", {"points": [v(-167.64, -48.05) * mm, v(-166.89, -49.5) * mm, v(-167, -51) * mm, v(-167.13, -52.46) * mm]});
            skFitSpline(sketch, "E497", {"points": [v(-167.13, -52.46) * mm, v(-167.53, -57.25) * mm, v(-169.86, -60.74) * mm, v(-174.3, -62.7) * mm]});
            skFitSpline(sketch, "E498", {"points": [v(-174.3, -62.7) * mm, v(-177.15, -63.95) * mm, v(-180.13, -64.2) * mm, v(-183.15, -63.51) * mm]});
            skFitSpline(sketch, "E499", {"points": [v(-183.15, -63.51) * mm, v(-185.97, -62.87) * mm, v(-188.29, -61.42) * mm, v(-189.74, -58.84) * mm]});
            skFitSpline(sketch, "E500", {"points": [v(-189.74, -58.84) * mm, v(-191.72, -55.32) * mm, v(-191.85, -51.56) * mm, v(-190.48, -47.88) * mm]});
            skFitSpline(sketch, "E501", {"points": [v(-190.48, -47.88) * mm, v(-188.56, -42.72) * mm, v(-184.75, -39.3) * mm, v(-179.72, -37.15) * mm]});
            skFitSpline(sketch, "E502", {"points": [v(-179.72, -37.15) * mm, v(-176.28, -35.7) * mm, v(-172.59, -35.38) * mm, v(-168.98, -34.67) * mm]});
            skFitSpline(sketch, "E503", {"points": [v(-168.98, -34.67) * mm, v(-164.57, -33.8) * mm, v(-160.18, -32.93) * mm, v(-155.98, -31.26) * mm]});
            skFitSpline(sketch, "E504", {"points": [v(-155.98, -31.26) * mm, v(-155.56, -31.1) * mm, v(-155.11, -31.01) * mm, v(-154.5, -30.84) * mm]});
            skFitSpline(sketch, "E505", {"points": [v(-154.5, -30.84) * mm, v(-159.21, -45.78) * mm, v(-163.85, -60.49) * mm, v(-168.54, -75.34) * mm]});
            skFitSpline(sketch, "E506", {"points": [v(-168.54, -75.34) * mm, v(-169.58, -75.34) * mm, v(-170.58, -75.3) * mm, v(-171.57, -75.35) * mm]});
            skFitSpline(sketch, "E507", {"points": [v(-171.57, -75.35) * mm, v(-172.54, -75.4) * mm, v(-173.57, -75.08) * mm, v(-174.47, -75.76) * mm]});
            skFitSpline(sketch, "E508", {"points": [v(-174.47, -75.76) * mm, v(-173.95, -75.94) * mm, v(-173.44, -75.98) * mm, v(-172.93, -75.98) * mm]});
            skFitSpline(sketch, "E509", {"points": [v(-172.93, -75.98) * mm, v(-167.47, -75.99) * mm, v(-162.01, -75.98) * mm, v(-156.55, -76) * mm]});
            skFitSpline(sketch, "E510", {"points": [v(-156.55, -76) * mm, v(-154.2, -76) * mm, v(-151.87, -75.8) * mm, v(-149.6, -75.14) * mm]});
            skFitSpline(sketch, "E511", {"points": [v(-149.6, -75.14) * mm, v(-141.22, -72.7) * mm, v(-135.55, -67.57) * mm, v(-133.67, -58.8) * mm]});
            skFitSpline(sketch, "E512", {"points": [v(-133.67, -58.8) * mm, v(-133.04, -55.89) * mm, v(-133.53, -53.04) * mm, v(-135.07, -50.5) * mm]});
            skFitSpline(sketch, "E513", {"points": [v(-135.07, -50.5) * mm, v(-136.8, -47.67) * mm, v(-139.4, -45.97) * mm, v(-142.6, -45.17) * mm]});
            skFitSpline(sketch, "E514", {"points": [v(-142.6, -45.17) * mm, v(-143.22, -45.02) * mm, v(-143.83, -44.89) * mm, v(-144.43, -44.74) * mm]});
            skFitSpline(sketch, "E515", {"points": [v(-144.43, -44.74) * mm, v(-141.65, -43.92) * mm, v(-139.02, -42.93) * mm, v(-136.65, -41.36) * mm]});
            skFitSpline(sketch, "E516", {"points": [v(-136.65, -41.36) * mm, v(-133.3, -39.14) * mm, v(-130.8, -36.26) * mm, v(-130.14, -32.15) * mm]});
            skFitSpline(sketch, "E517", {"points": [v(-130.14, -32.15) * mm, v(-129.66, -29.13) * mm, v(-130.54, -26.45) * mm, v(-133.04, -24.66) * mm]});
            skFitSpline(sketch, "E518", {"points": [v(-133.04, -24.66) * mm, v(-136.57, -22.12) * mm, v(-140.44, -21.76) * mm, v(-144.42, -23.67) * mm]});
            skFitSpline(sketch, "E519", {"points": [v(-144.42, -23.67) * mm, v(-145.3, -24.09) * mm, v(-146.16, -24.58) * mm, v(-147.25, -25.16) * mm]});
            skFitSpline(sketch, "E520", {"points": [v(-147.25, -25.16) * mm, v(-147.05, -24.24) * mm, v(-146.78, -23.55) * mm, v(-146.8, -22.87) * mm]});
            skFitSpline(sketch, "E521", {"points": [v(-146.8, -22.87) * mm, v(-146.87, -19.47) * mm, v(-149, -16.83) * mm, v(-152.57, -16.96) * mm]});
            skFitSpline(sketch, "E522", {"points": [v(-140.16, -23.2) * mm, v(-138.37, -23.15) * mm, v(-136.73, -23.7) * mm, v(-135.54, -25.25) * mm]});
            skFitSpline(sketch, "E523", {"points": [v(-135.54, -25.25) * mm, v(-134.68, -26.36) * mm, v(-134.16, -27.64) * mm, v(-134.11, -29.08) * mm]});
            skFitSpline(sketch, "E524", {"points": [v(-134.11, -29.08) * mm, v(-133.96, -33.83) * mm, v(-135.95, -37.64) * mm, v(-139.49, -40.61) * mm]});
            skFitSpline(sketch, "E525", {"points": [v(-139.49, -40.61) * mm, v(-143.35, -43.85) * mm, v(-147.94, -44.87) * mm, v(-152.9, -44.54) * mm]});
            skFitSpline(sketch, "E526", {"points": [v(-152.9, -44.54) * mm, v(-152.98, -44.53) * mm, v(-153.06, -44.46) * mm, v(-153.14, -44.41) * mm]});
            skFitSpline(sketch, "E527", {"points": [v(-153.14, -44.41) * mm, v(-153.17, -43.54) * mm, v(-149.1, -30.28) * mm, v(-147.62, -26.47) * mm]});
            skFitSpline(sketch, "E528", {"points": [v(-147.62, -26.47) * mm, v(-145.68, -24.93) * mm, v(-143.53, -23.58) * mm, v(-140.93, -23.27) * mm]});
            skFitSpline(sketch, "E529", {"points": [v(-140.93, -23.27) * mm, v(-140.67, -23.24) * mm, v(-140.41, -23.22) * mm, v(-140.16, -23.2) * mm]});
            skFitSpline(sketch, "E530", {"points": [v(-153.64, -45.2) * mm, v(-151.72, -45.2) * mm, v(-150.04, -45.18) * mm, v(-148.37, -45.2) * mm]});
            skFitSpline(sketch, "E531", {"points": [v(-148.37, -45.2) * mm, v(-146.73, -45.22) * mm, v(-145.13, -45.57) * mm, v(-143.71, -46.41) * mm]});
            skFitSpline(sketch, "E532", {"points": [v(-143.71, -46.41) * mm, v(-140.8, -48.15) * mm, v(-139.36, -50.86) * mm, v(-139.27, -54.15) * mm]});
            skFitSpline(sketch, "E533", {"points": [v(-139.27, -54.15) * mm, v(-139.04, -62.38) * mm, v(-142.53, -68.73) * mm, v(-149.45, -73.14) * mm]});
            skFitSpline(sketch, "E534", {"points": [v(-149.45, -73.14) * mm, v(-151.24, -74.27) * mm, v(-153.27, -74.92) * mm, v(-155.4, -75.07) * mm]});
            skFitSpline(sketch, "E535", {"points": [v(-155.4, -75.07) * mm, v(-157.73, -75.24) * mm, v(-160.07, -75.26) * mm, v(-162.4, -75.34) * mm]});
            skFitSpline(sketch, "E536", {"points": [v(-162.4, -75.34) * mm, v(-162.64, -75.34) * mm, v(-162.87, -75.3) * mm, v(-163.22, -75.26) * mm]});
            skFitSpline(sketch, "E537", {"points": [v(-163.22, -75.26) * mm, v(-160.01, -65.18) * mm, v(-156.82, -55.18) * mm, v(-153.64, -45.2) * mm]});
            skFitSpline(sketch, "E538", {"points": [v(-99.2, -47.84) * mm, v(-99.64, -47.84) * mm, v(-100.05, -47.95) * mm, v(-100.27, -48.68) * mm]});
            skLineSegment(sketch, "E539", {"start": v(-100.27, -48.68) * mm, "end": v(-93.66, -48.68) * mm});
            skFitSpline(sketch, "E540", {"points": [v(-93.66, -48.68) * mm, v(-95.45, -49.45) * mm, v(-96.63, -50.68) * mm, v(-97.25, -52.45) * mm]});
            skFitSpline(sketch, "E541", {"points": [v(-97.25, -52.45) * mm, v(-97.46, -53.04) * mm, v(-97.67, -53.62) * mm, v(-97.84, -54.22) * mm]});
            skFitSpline(sketch, "E542", {"points": [v(-97.84, -54.22) * mm, v(-98.63, -56.92) * mm, v(-99.4, -59.63) * mm, v(-100.18, -62.34) * mm]});
            skFitSpline(sketch, "E543", {"points": [v(-100.18, -62.34) * mm, v(-100.8, -64.5) * mm, v(-101.46, -66.65) * mm, v(-102.02, -68.82) * mm]});
            skFitSpline(sketch, "E544", {"points": [v(-102.02, -68.82) * mm, v(-102.43, -70.38) * mm, v(-102.22, -71.9) * mm, v(-101.14, -73.14) * mm]});
            skFitSpline(sketch, "E545", {"points": [v(-101.14, -73.14) * mm, v(-99.24, -75.32) * mm, v(-96.78, -76.02) * mm, v(-94.01, -75.43) * mm]});
            skFitSpline(sketch, "E546", {"points": [v(-94.01, -75.43) * mm, v(-91.15, -74.82) * mm, v(-89.64, -72.69) * mm, v(-88.61, -70.15) * mm]});
            skFitSpline(sketch, "E547", {"points": [v(-88.61, -70.15) * mm, v(-88.33, -69.43) * mm, v(-88.21, -68.64) * mm, v(-87.95, -67.6) * mm]});
            skFitSpline(sketch, "E548", {"points": [v(-87.95, -67.6) * mm, v(-88.82, -68.33) * mm, v(-88.76, -68.34) * mm, v(-88.97, -69.07) * mm]});
            skFitSpline(sketch, "E549", {"points": [v(-88.97, -69.07) * mm, v(-89.8, -71.8) * mm, v(-91.2, -74.03) * mm, v(-94.2, -74.8) * mm]});
            skFitSpline(sketch, "E550", {"points": [v(-94.2, -74.8) * mm, v(-96.1, -75.29) * mm, v(-97.29, -74.5) * mm, v(-97.22, -72.57) * mm]});
            skFitSpline(sketch, "E551", {"points": [v(-97.22, -72.57) * mm, v(-97.17, -71.25) * mm, v(-96.9, -69.91) * mm, v(-96.56, -68.63) * mm]});
            skFitSpline(sketch, "E552", {"points": [v(-96.56, -68.63) * mm, v(-95.84, -65.96) * mm, v(-95, -63.31) * mm, v(-94.24, -60.65) * mm]});
            skFitSpline(sketch, "E553", {"points": [v(-94.24, -60.65) * mm, v(-93.17, -56.94) * mm, v(-90.5, -47.9) * mm, v(-90.59, -47.9) * mm]});
            skFitSpline(sketch, "E554", {"points": [v(-90.59, -47.9) * mm, v(-93.22, -47.87) * mm, v(-96.57, -47.85) * mm, v(-99.2, -47.84) * mm]});
            skFitSpline(sketch, "E555", {"points": [v(-88.94, -29.07) * mm, v(-90.69, -29.13) * mm, v(-92.21, -31.17) * mm, v(-92.16, -32.5) * mm]});
            skFitSpline(sketch, "E556", {"points": [v(-92.16, -32.5) * mm, v(-92.09, -34.24) * mm, v(-90.47, -35.52) * mm, v(-88.8, -35.05) * mm]});
            skFitSpline(sketch, "E557", {"points": [v(-88.8, -35.05) * mm, v(-87.62, -34.71) * mm, v(-86.72, -33.98) * mm, v(-86.28, -32.86) * mm]});
            skFitSpline(sketch, "E558", {"points": [v(-86.28, -32.86) * mm, v(-85.42, -30.71) * mm, v(-86.97, -28.9) * mm, v(-88.6, -29.08) * mm]});
            skFitSpline(sketch, "E559", {"points": [v(-88.6, -29.08) * mm, v(-88.71, -29.07) * mm, v(-88.83, -29.06) * mm, v(-88.94, -29.07) * mm]});
            skFitSpline(sketch, "E560", {"points": [v(-108.87, -47.66) * mm, v(-110.3, -47.6) * mm, v(-111.65, -48) * mm, v(-112.9, -48.74) * mm]});
            skFitSpline(sketch, "E561", {"points": [v(-112.9, -48.74) * mm, v(-115.35, -50.2) * mm, v(-117.14, -52.28) * mm, v(-118.86, -54.61) * mm]});
            skFitSpline(sketch, "E562", {"points": [v(-118.86, -54.61) * mm, v(-118.27, -52.43) * mm, v(-117.67, -50.26) * mm, v(-117.03, -47.92) * mm]});
            skFitSpline(sketch, "E563", {"points": [v(-117.03, -47.92) * mm, v(-117.74, -47.88) * mm, v(-124.74, -47.82) * mm, v(-125.67, -47.81) * mm]});
            skFitSpline(sketch, "E564", {"points": [v(-125.67, -47.81) * mm, v(-126.11, -47.81) * mm, v(-126.52, -47.93) * mm, v(-126.74, -48.65) * mm]});
            skFitSpline(sketch, "E565", {"points": [v(-126.74, -48.65) * mm, v(-126.62, -48.65) * mm, v(-122.38, -48.65) * mm, v(-120.37, -48.65) * mm]});
            skFitSpline(sketch, "E566", {"points": [v(-120.37, -48.65) * mm, v(-122.46, -49.76) * mm, v(-123.46, -51.52) * mm, v(-124.06, -53.64) * mm]});
            skFitSpline(sketch, "E567", {"points": [v(-124.06, -53.64) * mm, v(-125.66, -59.34) * mm, v(-127.3, -65.04) * mm, v(-128.93, -70.74) * mm]});
            skFitSpline(sketch, "E568", {"points": [v(-128.93, -70.74) * mm, v(-129.34, -72.2) * mm, v(-129.73, -73.65) * mm, v(-130.13, -75.1) * mm]});
            skFitSpline(sketch, "E569", {"points": [v(-130.13, -75.1) * mm, v(-128.85, -75.56) * mm, v(-125.97, -75.56) * mm, v(-124.75, -75.14) * mm]});
            skFitSpline(sketch, "E570", {"points": [v(-124.75, -75.14) * mm, v(-124.66, -74.91) * mm, v(-124.55, -74.65) * mm, v(-124.47, -74.38) * mm]});
            skFitSpline(sketch, "E571", {"points": [v(-124.47, -74.38) * mm, v(-123.63, -71.5) * mm, v(-122.8, -68.6) * mm, v(-121.96, -65.71) * mm]});
            skFitSpline(sketch, "E572", {"points": [v(-121.96, -65.71) * mm, v(-121.09, -62.69) * mm, v(-120.38, -59.62) * mm, v(-118.93, -56.77) * mm]});
            skFitSpline(sketch, "E573", {"points": [v(-118.93, -56.77) * mm, v(-117.65, -54.25) * mm, v(-116.04, -52.04) * mm, v(-113.87, -50.24) * mm]});
            skFitSpline(sketch, "E574", {"points": [v(-113.87, -50.24) * mm, v(-112.32, -48.96) * mm, v(-110.54, -48.18) * mm, v(-108.46, -48.4) * mm]});
            skFitSpline(sketch, "E575", {"points": [v(-108.46, -48.4) * mm, v(-107.5, -48.48) * mm, v(-107, -48.8) * mm, v(-106.84, -49.53) * mm]});
            skFitSpline(sketch, "E576", {"points": [v(-106.84, -49.53) * mm, v(-106.65, -50.43) * mm, v(-106.65, -51.35) * mm, v(-107.14, -52.18) * mm]});
            skFitSpline(sketch, "E577", {"points": [v(-107.14, -52.18) * mm, v(-108.29, -54.14) * mm, v(-109.94, -55.28) * mm, v(-112.27, -55.29) * mm]});
            skFitSpline(sketch, "E578", {"points": [v(-112.27, -55.29) * mm, v(-112.83, -55.29) * mm, v(-113.39, -55.29) * mm, v(-113.88, -55.29) * mm]});
            skFitSpline(sketch, "E579", {"points": [v(-113.88, -55.29) * mm, v(-114.42, -57.06) * mm, v(-113.73, -58.54) * mm, v(-112.22, -59.01) * mm]});
            skFitSpline(sketch, "E580", {"points": [v(-112.22, -59.01) * mm, v(-110.31, -59.6) * mm, v(-108.61, -59.03) * mm, v(-107.15, -57.8) * mm]});
            skFitSpline(sketch, "E581", {"points": [v(-107.15, -57.8) * mm, v(-105.32, -56.26) * mm, v(-104.53, -54.16) * mm, v(-104.5, -51.83) * mm]});
            skFitSpline(sketch, "E582", {"points": [v(-104.5, -51.83) * mm, v(-104.47, -49.57) * mm, v(-105.99, -47.98) * mm, v(-108.25, -47.7) * mm]});
            skFitSpline(sketch, "E583", {"points": [v(-108.25, -47.7) * mm, v(-108.46, -47.68) * mm, v(-108.67, -47.66) * mm, v(-108.87, -47.66) * mm]});
            skFitSpline(sketch, "E584", {"points": [v(-10, -34.73) * mm, v(-10.43, -34.73) * mm, v(-10.84, -34.84) * mm, v(-11.06, -35.56) * mm]});
            skLineSegment(sketch, "E585", {"start": v(-11.06, -35.56) * mm, "end": v(-3.86, -35.56) * mm});
            skFitSpline(sketch, "E586", {"points": [v(-3.86, -35.56) * mm, v(-3.73, -35.57) * mm, v(-3.6, -35.57) * mm, v(-3.47, -35.58) * mm]});
            skFitSpline(sketch, "E587", {"points": [v(-3.47, -35.58) * mm, v(-4.99, -37.25) * mm, v(-5.6, -39.25) * mm, v(-6.08, -41.3) * mm]});
            skFitSpline(sketch, "E588", {"points": [v(-6.08, -41.3) * mm, v(-6.16, -41.63) * mm, v(-6.25, -41.95) * mm, v(-6.34, -42.27) * mm]});
            skFitSpline(sketch, "E589", {"points": [v(-6.34, -42.27) * mm, v(-8.56, -49.93) * mm, v(-10.8, -57.6) * mm, v(-13, -65.27) * mm]});
            skFitSpline(sketch, "E590", {"points": [v(-13, -65.27) * mm, v(-13.47, -66.95) * mm, v(-14.14, -68.6) * mm, v(-14.03, -70.44) * mm]});
            skFitSpline(sketch, "E591", {"points": [v(-14.03, -70.44) * mm, v(-13.91, -72.22) * mm, v(-13.15, -73.58) * mm, v(-11.6, -74.4) * mm]});
            skFitSpline(sketch, "E592", {"points": [v(-11.6, -74.4) * mm, v(-10.74, -74.87) * mm, v(-9.75, -75.15) * mm, v(-8.8, -75.44) * mm]});
            skFitSpline(sketch, "E593", {"points": [v(-8.8, -75.44) * mm, v(-6.68, -76.07) * mm, v(-4.74, -75.5) * mm, v(-3.17, -74.13) * mm]});
            skFitSpline(sketch, "E594", {"points": [v(-3.17, -74.13) * mm, v(-0.4, -71.72) * mm, v(0.73, -68.54) * mm, v(0.4, -64.87) * mm]});
            skFitSpline(sketch, "E595", {"points": [v(0.4, -64.87) * mm, v(0.38, -64.56) * mm, v(0.16, -64.26) * mm, v(0.02, -63.96) * mm]});
            skFitSpline(sketch, "E596", {"points": [v(0.02, -63.96) * mm, v(-0.07, -63.98) * mm, v(-0.16, -64) * mm, v(-0.26, -64.02) * mm]});
            skFitSpline(sketch, "E597", {"points": [v(-0.26, -64.02) * mm, v(-0.3, -64.23) * mm, v(-0.45, -64.46) * mm, v(-0.4, -64.64) * mm]});
            skFitSpline(sketch, "E598", {"points": [v(-0.4, -64.64) * mm, v(0.2, -66.88) * mm, v(-0.46, -68.93) * mm, v(-1.44, -70.87) * mm]});
            skFitSpline(sketch, "E599", {"points": [v(-1.44, -70.87) * mm, v(-2.46, -72.91) * mm, v(-4.02, -74.42) * mm, v(-6.37, -74.9) * mm]});
            skFitSpline(sketch, "E600", {"points": [v(-6.37, -74.9) * mm, v(-7.83, -75.21) * mm, v(-8.97, -74.42) * mm, v(-9.07, -72.94) * mm]});
            skFitSpline(sketch, "E601", {"points": [v(-9.07, -72.94) * mm, v(-9.16, -71.6) * mm, v(-9, -70.29) * mm, v(-8.61, -68.98) * mm]});
            skFitSpline(sketch, "E602", {"points": [v(-8.61, -68.98) * mm, v(-6.98, -63.43) * mm, v(-5.4, -57.87) * mm, v(-3.8, -52.32) * mm]});
            skFitSpline(sketch, "E603", {"points": [v(-3.8, -52.32) * mm, v(-2.44, -47.6) * mm, v(1.14, -34.96) * mm, v(1.35, -34.75) * mm]});
            skFitSpline(sketch, "E604", {"points": [v(1.35, -34.75) * mm, v(0.21, -34.75) * mm, v(-8.85, -34.73) * mm, v(-10, -34.73) * mm]});
            skFitSpline(sketch, "E605", {"points": [v(51.3, -21.69) * mm, v(50.02, -21.68) * mm, v(48.73, -21.84) * mm, v(47.44, -22.17) * mm]});
            skFitSpline(sketch, "E606", {"points": [v(47.44, -22.17) * mm, v(43.04, -23.26) * mm, v(39.85, -25.84) * mm, v(38.12, -30.13) * mm]});
            skFitSpline(sketch, "E607", {"points": [v(38.12, -30.13) * mm, v(36.75, -33.5) * mm, v(37.4, -36.71) * mm, v(38.83, -39.85) * mm]});
            skFitSpline(sketch, "E608", {"points": [v(38.83, -39.85) * mm, v(40.41, -43.3) * mm, v(42.7, -46.33) * mm, v(44.8, -49.47) * mm]});
            skFitSpline(sketch, "E609", {"points": [v(44.8, -49.47) * mm, v(46.61, -52.18) * mm, v(48.36, -54.93) * mm, v(49.3, -58.09) * mm]});
            skFitSpline(sketch, "E610", {"points": [v(49.3, -58.09) * mm, v(50.56, -62.31) * mm, v(50.2, -66.3) * mm, v(47.4, -69.9) * mm]});
            skFitSpline(sketch, "E611", {"points": [v(47.4, -69.9) * mm, v(43.6, -74.79) * mm, v(35.77, -75.92) * mm, v(30.63, -72.67) * mm]});
            skFitSpline(sketch, "E612", {"points": [v(30.63, -72.67) * mm, v(27.8, -70.88) * mm, v(26.24, -68.32) * mm, v(26.37, -64.89) * mm]});
            skFitSpline(sketch, "E613", {"points": [v(26.37, -64.89) * mm, v(26.41, -63.8) * mm, v(26.47, -62.67) * mm, v(26.75, -61.62) * mm]});
            skFitSpline(sketch, "E614", {"points": [v(26.75, -61.62) * mm, v(27.67, -58.14) * mm, v(29.24, -55.1) * mm, v(32.82, -53.6) * mm]});
            skFitSpline(sketch, "E615", {"points": [v(32.82, -53.6) * mm, v(33.03, -53.5) * mm, v(33.2, -53.32) * mm, v(33.38, -53.2) * mm]});
            skFitSpline(sketch, "E616", {"points": [v(33.38, -53.2) * mm, v(32.66, -51.75) * mm, v(31.6, -51.17) * mm, v(30.12, -51.47) * mm]});
            skFitSpline(sketch, "E617", {"points": [v(30.12, -51.47) * mm, v(28.59, -51.79) * mm, v(27.23, -52.48) * mm, v(26.08, -53.55) * mm]});
            skFitSpline(sketch, "E618", {"points": [v(26.08, -53.55) * mm, v(22.04, -57.3) * mm, v(20.72, -64.5) * mm, v(24.67, -69.47) * mm]});
            skFitSpline(sketch, "E619", {"points": [v(24.67, -69.47) * mm, v(28.26, -74) * mm, v(33.14, -75.33) * mm, v(38.6, -75.03) * mm]});
            skFitSpline(sketch, "E620", {"points": [v(38.6, -75.03) * mm, v(41.62, -74.87) * mm, v(44.52, -74) * mm, v(47.2, -72.5) * mm]});
            skFitSpline(sketch, "E621", {"points": [v(47.2, -72.5) * mm, v(53.77, -68.8) * mm, v(56.72, -62.84) * mm, v(54.46, -55.2) * mm]});
            skFitSpline(sketch, "E622", {"points": [v(54.46, -55.2) * mm, v(53.54, -52.09) * mm, v(51.94, -49.33) * mm, v(50.2, -46.63) * mm]});
            skFitSpline(sketch, "E623", {"points": [v(50.2, -46.63) * mm, v(48.32, -43.74) * mm, v(46.4, -40.89) * mm, v(44.58, -37.96) * mm]});
            skFitSpline(sketch, "E624", {"points": [v(44.58, -37.96) * mm, v(43.35, -35.95) * mm, v(42.47, -33.77) * mm, v(42.3, -31.37) * mm]});
            skFitSpline(sketch, "E625", {"points": [v(42.3, -31.37) * mm, v(42.08, -28.2) * mm, v(42.92, -25.4) * mm, v(45.82, -23.75) * mm]});
            skFitSpline(sketch, "E626", {"points": [v(45.82, -23.75) * mm, v(48.82, -22.04) * mm, v(52.02, -21.95) * mm, v(55.22, -23.23) * mm]});
            skFitSpline(sketch, "E627", {"points": [v(55.22, -23.23) * mm, v(56.22, -23.64) * mm, v(56.98, -24.4) * mm, v(57.48, -25.36) * mm]});
            skFitSpline(sketch, "E628", {"points": [v(57.48, -25.36) * mm, v(59.01, -28.35) * mm, v(58.9, -31.36) * mm, v(57.49, -34.33) * mm]});
            skFitSpline(sketch, "E629", {"points": [v(57.49, -34.33) * mm, v(56.99, -35.4) * mm, v(56.23, -36.34) * mm, v(55.6, -37.34) * mm]});
            skFitSpline(sketch, "E630", {"points": [v(55.6, -37.34) * mm, v(56.97, -38.48) * mm, v(58.28, -38.55) * mm, v(59.7, -37.4) * mm]});
            skFitSpline(sketch, "E631", {"points": [v(59.7, -37.4) * mm, v(62.2, -35.4) * mm, v(63.15, -32.7) * mm, v(62.7, -29.61) * mm]});
            skFitSpline(sketch, "E632", {"points": [v(62.7, -29.61) * mm, v(62.25, -26.53) * mm, v(60.21, -24.5) * mm, v(57.51, -23.16) * mm]});
            skFitSpline(sketch, "E633", {"points": [v(57.51, -23.16) * mm, v(55.5, -22.17) * mm, v(53.42, -21.7) * mm, v(51.3, -21.69) * mm]});
            skFitSpline(sketch, "E634", {"points": [v(183.73, -46.41) * mm, v(182.6, -46.45) * mm, v(181.47, -46.65) * mm, v(180.35, -47) * mm]});
            skFitSpline(sketch, "E635", {"points": [v(180.35, -47) * mm, v(176.84, -48.07) * mm, v(174.06, -50.18) * mm, v(171.87, -53.1) * mm]});
            skFitSpline(sketch, "E636", {"points": [v(171.87, -53.1) * mm, v(168.85, -57.14) * mm, v(167.1, -61.6) * mm, v(167.64, -66.73) * mm]});
            skFitSpline(sketch, "E637", {"points": [v(167.64, -66.73) * mm, v(167.97, -69.85) * mm, v(169.4, -72.33) * mm, v(172.36, -73.58) * mm]});
            skFitSpline(sketch, "E638", {"points": [v(172.36, -73.58) * mm, v(173.74, -74.17) * mm, v(175.3, -74.3) * mm, v(176.67, -74.62) * mm]});
            skFitSpline(sketch, "E639", {"points": [v(176.67, -74.62) * mm, v(178.17, -74.34) * mm, v(179.5, -74.2) * mm, v(180.78, -73.84) * mm]});
            skFitSpline(sketch, "E640", {"points": [v(180.78, -73.84) * mm, v(184.08, -72.91) * mm, v(186.69, -70.91) * mm, v(188.81, -68.3) * mm]});
            skFitSpline(sketch, "E641", {"points": [v(188.81, -68.3) * mm, v(191.92, -64.47) * mm, v(193.76, -60.13) * mm, v(193.59, -55.1) * mm]});
            skFitSpline(sketch, "E642", {"points": [v(193.59, -55.1) * mm, v(193.44, -50.88) * mm, v(190.96, -47.7) * mm, v(187.15, -46.77) * mm]});
            skFitSpline(sketch, "E643", {"points": [v(187.15, -46.77) * mm, v(186, -46.5) * mm, v(184.87, -46.38) * mm, v(183.73, -46.41) * mm]});
            skFitSpline(sketch, "E644", {"points": [v(184.15, -46.98) * mm, v(184.33, -46.98) * mm, v(184.5, -47) * mm, v(184.69, -47.02) * mm]});
            skFitSpline(sketch, "E645", {"points": [v(184.69, -47.02) * mm, v(186.55, -47.23) * mm, v(187.96, -48.48) * mm, v(188.37, -50.34) * mm]});
            skFitSpline(sketch, "E646", {"points": [v(188.37, -50.34) * mm, v(188.63, -51.55) * mm, v(188.73, -52.8) * mm, v(188.85, -53.67) * mm]});
            skFitSpline(sketch, "E647", {"points": [v(188.85, -53.67) * mm, v(188.46, -60.29) * mm, v(186.46, -65.91) * mm, v(182.47, -70.76) * mm]});
            skFitSpline(sketch, "E648", {"points": [v(182.47, -70.76) * mm, v(181.27, -72.2) * mm, v(179.78, -73.33) * mm, v(177.87, -73.8) * mm]});
            skFitSpline(sketch, "E649", {"points": [v(177.87, -73.8) * mm, v(175.85, -74.28) * mm, v(174, -73.37) * mm, v(173.23, -71.43) * mm]});
            skFitSpline(sketch, "E650", {"points": [v(173.23, -71.43) * mm, v(172.3, -69.12) * mm, v(172.42, -66.72) * mm, v(172.8, -64.35) * mm]});
            skFitSpline(sketch, "E651", {"points": [v(172.8, -64.35) * mm, v(173.53, -59.72) * mm, v(175.09, -55.37) * mm, v(177.82, -51.52) * mm]});
            skFitSpline(sketch, "E652", {"points": [v(177.82, -51.52) * mm, v(178.67, -50.33) * mm, v(179.74, -49.26) * mm, v(180.85, -48.3) * mm]});
            skFitSpline(sketch, "E653", {"points": [v(180.85, -48.3) * mm, v(181.78, -47.48) * mm, v(182.9, -46.98) * mm, v(184.15, -46.98) * mm]});
            skFitSpline(sketch, "E654", {"points": [v(162.82, -28.06) * mm, v(160.98, -28.05) * mm, v(159.32, -29.71) * mm, v(159.36, -31.52) * mm]});
            skFitSpline(sketch, "E655", {"points": [v(159.36, -31.52) * mm, v(159.4, -32.9) * mm, v(160.56, -34) * mm, v(162, -34) * mm]});
            skFitSpline(sketch, "E656", {"points": [v(162, -34) * mm, v(163.76, -34) * mm, v(165.33, -32.39) * mm, v(165.32, -30.57) * mm]});
            skFitSpline(sketch, "E657", {"points": [v(165.32, -30.57) * mm, v(165.3, -29.06) * mm, v(164.32, -28.06) * mm, v(162.82, -28.06) * mm]});
            skFitSpline(sketch, "E658", {"points": [v(-62.82, -34.73) * mm, v(-63.26, -34.73) * mm, v(-63.67, -34.84) * mm, v(-63.89, -35.56) * mm]});
            skLineSegment(sketch, "E659", {"start": v(-63.89, -35.56) * mm, "end": v(-55.95, -35.56) * mm});
            skFitSpline(sketch, "E660", {"points": [v(-55.95, -35.56) * mm, v(-57.3, -36.7) * mm, v(-57.82, -38.02) * mm, v(-58.22, -39.4) * mm]});
            skFitSpline(sketch, "E661", {"points": [v(-58.22, -39.4) * mm, v(-59.5, -43.8) * mm, v(-60.73, -48.22) * mm, v(-61.98, -52.63) * mm]});
            skFitSpline(sketch, "E662", {"points": [v(-61.98, -52.63) * mm, v(-62.05, -52.85) * mm, v(-62.17, -53.06) * mm, v(-62.27, -53.27) * mm]});
            skFitSpline(sketch, "E663", {"points": [v(-62.27, -53.27) * mm, v(-62.46, -52.9) * mm, v(-62.42, -52.55) * mm, v(-62.5, -52.24) * mm]});
            skFitSpline(sketch, "E664", {"points": [v(-62.5, -52.24) * mm, v(-63.15, -49.32) * mm, v(-64.6, -47.64) * mm, v(-67.48, -47.64) * mm]});
            skFitSpline(sketch, "E665", {"points": [v(-67.48, -47.64) * mm, v(-69.46, -47.64) * mm, v(-71.35, -48.11) * mm, v(-73.13, -49.06) * mm]});
            skFitSpline(sketch, "E666", {"points": [v(-73.13, -49.06) * mm, v(-77.46, -51.37) * mm, v(-80.3, -55.01) * mm, v(-82.38, -59.33) * mm]});
            skFitSpline(sketch, "E667", {"points": [v(-82.38, -59.33) * mm, v(-83.7, -62.08) * mm, v(-84.46, -64.98) * mm, v(-84.33, -68.06) * mm]});
            skFitSpline(sketch, "E668", {"points": [v(-84.33, -68.06) * mm, v(-84.13, -72.65) * mm, v(-81.06, -75.62) * mm, v(-76.49, -75.68) * mm]});
            skFitSpline(sketch, "E669", {"points": [v(-76.49, -75.68) * mm, v(-75.46, -75.7) * mm, v(-74.5, -75.54) * mm, v(-73.57, -75.1) * mm]});
            skFitSpline(sketch, "E670", {"points": [v(-73.57, -75.1) * mm, v(-71.57, -74.18) * mm, v(-69.96, -72.79) * mm, v(-68.57, -71.11) * mm]});
            skFitSpline(sketch, "E671", {"points": [v(-68.57, -71.11) * mm, v(-67.94, -70.35) * mm, v(-67.36, -69.54) * mm, v(-66.6, -68.54) * mm]});
            skFitSpline(sketch, "E672", {"points": [v(-66.6, -68.54) * mm, v(-66.6, -69.25) * mm, v(-66.6, -69.7) * mm, v(-66.6, -70.16) * mm]});
            skFitSpline(sketch, "E673", {"points": [v(-66.6, -70.16) * mm, v(-66.6, -72.43) * mm, v(-65.47, -73.95) * mm, v(-63.46, -74.87) * mm]});
            skFitSpline(sketch, "E674", {"points": [v(-63.46, -74.87) * mm, v(-63.02, -75.06) * mm, v(-62.57, -75.25) * mm, v(-62.12, -75.38) * mm]});
            skFitSpline(sketch, "E675", {"points": [v(-62.12, -75.38) * mm, v(-60.51, -75.83) * mm, v(-59.04, -75.8) * mm, v(-57.68, -75.29) * mm]});
            skFitSpline(sketch, "E676", {"points": [v(-57, -75) * mm, v(-55, -74.06) * mm, v(-53.82, -72.23) * mm, v(-53.01, -70.1) * mm]});
            skFitSpline(sketch, "E677", {"points": [v(-53.01, -70.1) * mm, v(-52.74, -69.38) * mm, v(-52.64, -68.6) * mm, v(-52.4, -67.55) * mm]});
            skFitSpline(sketch, "E678", {"points": [v(-52.4, -67.55) * mm, v(-53.25, -68.29) * mm, v(-53.2, -68.3) * mm, v(-53.4, -69.03) * mm]});
            skFitSpline(sketch, "E679", {"points": [v(-53.4, -69.03) * mm, v(-54.05, -71.42) * mm, v(-55.17, -73.41) * mm, v(-57.4, -74.44) * mm]});
            skFitSpline(sketch, "E680", {"points": [v(-58.05, -74.75) * mm, v(-60.15, -75.58) * mm, v(-61.67, -74.67) * mm, v(-61.64, -72.45) * mm]});
            skFitSpline(sketch, "E681", {"points": [v(-61.64, -72.45) * mm, v(-61.62, -71.31) * mm, v(-61.46, -70.15) * mm, v(-61.17, -69.06) * mm]});
            skFitSpline(sketch, "E682", {"points": [v(-61.17, -69.06) * mm, v(-60.35, -65.96) * mm, v(-59.4, -62.9) * mm, v(-58.55, -59.82) * mm]});
            skFitSpline(sketch, "E683", {"points": [v(-58.55, -59.82) * mm, v(-56.68, -53.14) * mm, v(-54.84, -46.46) * mm, v(-52.99, -39.78) * mm]});
            skFitSpline(sketch, "E684", {"points": [v(-52.99, -39.78) * mm, v(-52.56, -38.24) * mm, v(-51.7, -34.85) * mm, v(-51.58, -34.73) * mm]});
            skFitSpline(sketch, "E685", {"points": [v(-51.58, -34.73) * mm, v(-52.72, -34.72) * mm, v(-61.68, -34.73) * mm, v(-62.82, -34.73) * mm]});
            skFitSpline(sketch, "E686", {"points": [v(-67.27, -48.34) * mm, v(-66.1, -48.38) * mm, v(-65, -48.84) * mm, v(-64.23, -49.73) * mm]});
            skFitSpline(sketch, "E687", {"points": [v(-64.23, -49.73) * mm, v(-63.48, -50.6) * mm, v(-63.21, -51.66) * mm, v(-63.1, -52.77) * mm]});
            skFitSpline(sketch, "E688", {"points": [v(-63.1, -52.77) * mm, v(-63.05, -53.33) * mm, v(-63.1, -53.91) * mm, v(-63.1, -54.49) * mm]});
            skFitSpline(sketch, "E689", {"points": [v(-63.1, -54.49) * mm, v(-63.02, -54.5) * mm, v(-62.94, -54.51) * mm, v(-62.86, -54.53) * mm]});
            skFitSpline(sketch, "E690", {"points": [v(-62.86, -54.53) * mm, v(-63.14, -55.92) * mm, v(-63.32, -57.34) * mm, v(-63.71, -58.7) * mm]});
            skFitSpline(sketch, "E691", {"points": [v(-63.71, -58.7) * mm, v(-64.4, -61.13) * mm, v(-65.03, -63.6) * mm, v(-66.06, -65.9) * mm]});
            skFitSpline(sketch, "E692", {"points": [v(-66.06, -65.9) * mm, v(-67.68, -69.54) * mm, v(-70.14, -72.56) * mm, v(-73.8, -74.42) * mm]});
            skFitSpline(sketch, "E693", {"points": [v(-73.8, -74.42) * mm, v(-74.14, -74.6) * mm, v(-74.5, -74.74) * mm, v(-74.86, -74.85) * mm]});
            skFitSpline(sketch, "E694", {"points": [v(-74.86, -74.85) * mm, v(-76.6, -75.38) * mm, v(-78.24, -74.57) * mm, v(-78.91, -72.87) * mm]});
            skFitSpline(sketch, "E695", {"points": [v(-78.91, -72.87) * mm, v(-79.68, -70.93) * mm, v(-79.6, -68.9) * mm, v(-79.29, -66.93) * mm]});
            skFitSpline(sketch, "E696", {"points": [v(-79.29, -66.93) * mm, v(-78.53, -62.11) * mm, v(-76.84, -57.61) * mm, v(-74.22, -53.48) * mm]});
            skFitSpline(sketch, "E697", {"points": [v(-74.22, -53.48) * mm, v(-73.26, -51.98) * mm, v(-72.08, -50.67) * mm, v(-70.7, -49.55) * mm]});
            skFitSpline(sketch, "E698", {"points": [v(-70.7, -49.55) * mm, v(-69.66, -48.7) * mm, v(-68.43, -48.3) * mm, v(-67.27, -48.34) * mm]});
            skFitSpline(sketch, "E699", {"points": [v(-31.7, -47.67) * mm, v(-32.67, -47.64) * mm, v(-33.61, -47.76) * mm, v(-34.56, -48) * mm]});
            skFitSpline(sketch, "E700", {"points": [v(-34.56, -48) * mm, v(-37.7, -48.76) * mm, v(-40.2, -50.59) * mm, v(-42.36, -52.87) * mm]});
            skFitSpline(sketch, "E701", {"points": [v(-42.36, -52.87) * mm, v(-44.24, -54.86) * mm, v(-45.76, -57.13) * mm, v(-46.85, -59.66) * mm]});
            skFitSpline(sketch, "E702", {"points": [v(-46.85, -59.66) * mm, v(-48.04, -62.4) * mm, v(-48.9, -65.22) * mm, v(-48.73, -68.27) * mm]});
            skFitSpline(sketch, "E703", {"points": [v(-48.73, -68.27) * mm, v(-48.47, -72.58) * mm, v(-45.73, -75.43) * mm, v(-41.17, -75.68) * mm]});
            skFitSpline(sketch, "E704", {"points": [v(-41.17, -75.68) * mm, v(-38.83, -75.8) * mm, v(-36.96, -74.82) * mm, v(-35.36, -73.34) * mm]});
            skFitSpline(sketch, "E705", {"points": [v(-35.36, -73.34) * mm, v(-34.07, -72.15) * mm, v(-33, -70.72) * mm, v(-31.84, -69.4) * mm]});
            skFitSpline(sketch, "E706", {"points": [v(-31.84, -69.4) * mm, v(-31.58, -69.1) * mm, v(-31.32, -68.78) * mm, v(-30.95, -68.35) * mm]});
            skFitSpline(sketch, "E707", {"points": [v(-30.95, -68.35) * mm, v(-30.95, -69.12) * mm, v(-31, -69.7) * mm, v(-30.95, -70.26) * mm]});
            skFitSpline(sketch, "E708", {"points": [v(-30.95, -70.26) * mm, v(-30.84, -71.75) * mm, v(-30.34, -73.08) * mm, v(-29.17, -74.06) * mm]});
            skFitSpline(sketch, "E709", {"points": [v(-29.17, -74.06) * mm, v(-27, -75.9) * mm, v(-22.72, -76.55) * mm, v(-20.09, -74.03) * mm]});
            skFitSpline(sketch, "E710", {"points": [v(-20.09, -74.03) * mm, v(-20.08, -74.02) * mm, v(-20.08, -74.01) * mm, v(-20.07, -74) * mm]});
            skFitSpline(sketch, "E711", {"points": [v(-20.07, -74) * mm, v(-18.95, -73) * mm, v(-18.2, -71.62) * mm, v(-17.63, -70.1) * mm]});
            skFitSpline(sketch, "E712", {"points": [v(-17.63, -70.1) * mm, v(-17.36, -69.37) * mm, v(-17.27, -68.58) * mm, v(-17.03, -67.54) * mm]});
            skFitSpline(sketch, "E713", {"points": [v(-17.03, -67.54) * mm, v(-17.87, -68.28) * mm, v(-17.82, -68.3) * mm, v(-18.01, -69.03) * mm]});
            skFitSpline(sketch, "E714", {"points": [v(-18.01, -69.03) * mm, v(-18.5, -70.8) * mm, v(-19.23, -72.34) * mm, v(-20.47, -73.46) * mm]});
            skFitSpline(sketch, "E715", {"points": [v(-20.47, -73.46) * mm, v(-20.77, -73.72) * mm, v(-21.1, -73.97) * mm, v(-21.44, -74.17) * mm]});
            skFitSpline(sketch, "E716", {"points": [v(-21.44, -74.17) * mm, v(-21.45, -74.18) * mm, v(-21.46, -74.18) * mm, v(-21.46, -74.18) * mm]});
            skFitSpline(sketch, "E717", {"points": [v(-21.46, -74.18) * mm, v(-21.87, -74.42) * mm, v(-22.3, -74.62) * mm, v(-22.78, -74.78) * mm]});
            skFitSpline(sketch, "E718", {"points": [v(-22.78, -74.78) * mm, v(-24.94, -75.53) * mm, v(-26.32, -74.61) * mm, v(-26.21, -72.3) * mm]});
            skFitSpline(sketch, "E719", {"points": [v(-26.21, -72.3) * mm, v(-26.15, -71.09) * mm, v(-25.8, -69.87) * mm, v(-25.48, -68.68) * mm]});
            skFitSpline(sketch, "E720", {"points": [v(-25.48, -68.68) * mm, v(-23.66, -62.14) * mm, v(-19.88, -48.44) * mm, v(-19.8, -47.92) * mm]});
            skFitSpline(sketch, "E721", {"points": [v(-19.8, -47.92) * mm, v(-21.55, -47.77) * mm, v(-23.2, -47.8) * mm, v(-24.75, -47.9) * mm]});
            skFitSpline(sketch, "E722", {"points": [v(-24.75, -47.9) * mm, v(-24.93, -48.13) * mm, v(-26.07, -51.43) * mm, v(-26.56, -53) * mm]});
            skFitSpline(sketch, "E723", {"points": [v(-26.56, -53) * mm, v(-26.98, -51.85) * mm, v(-27.26, -50.73) * mm, v(-27.78, -49.74) * mm]});
            skFitSpline(sketch, "E724", {"points": [v(-27.78, -49.74) * mm, v(-28.37, -48.6) * mm, v(-29.38, -47.9) * mm, v(-30.73, -47.74) * mm]});
            skFitSpline(sketch, "E725", {"points": [v(-30.73, -47.74) * mm, v(-31.06, -47.7) * mm, v(-31.38, -47.67) * mm, v(-31.7, -47.67) * mm]});
            skFitSpline(sketch, "E726", {"points": [v(-31.76, -48.38) * mm, v(-29.69, -48.36) * mm, v(-28.4, -49.25) * mm, v(-27.84, -51.24) * mm]});
            skFitSpline(sketch, "E727", {"points": [v(-27.84, -51.24) * mm, v(-27.2, -53.5) * mm, v(-27.32, -55.78) * mm, v(-27.95, -58.03) * mm]});
            skFitSpline(sketch, "E728", {"points": [v(-27.95, -58.03) * mm, v(-28.57, -60.18) * mm, v(-29.16, -62.35) * mm, v(-29.9, -64.46) * mm]});
            skFitSpline(sketch, "E729", {"points": [v(-29.9, -64.46) * mm, v(-31.06, -67.72) * mm, v(-33.02, -70.49) * mm, v(-35.68, -72.7) * mm]});
            skFitSpline(sketch, "E730", {"points": [v(-35.68, -72.7) * mm, v(-36.62, -73.47) * mm, v(-37.75, -74.03) * mm, v(-38.82, -74.64) * mm]});
            skFitSpline(sketch, "E731", {"points": [v(-38.82, -74.64) * mm, v(-40.68, -75.7) * mm, v(-43.3, -74.8) * mm, v(-43.77, -71.67) * mm]});
            skFitSpline(sketch, "E732", {"points": [v(-43.77, -71.67) * mm, v(-43.88, -70.92) * mm, v(-43.78, -70.14) * mm, v(-43.78, -69.37) * mm]});
            skFitSpline(sketch, "E733", {"points": [v(-43.78, -69.37) * mm, v(-43.98, -66.3) * mm, v(-43.03, -63.42) * mm, v(-42.04, -60.59) * mm]});
            skFitSpline(sketch, "E734", {"points": [v(-42.04, -60.59) * mm, v(-40.78, -57) * mm, v(-39.07, -53.64) * mm, v(-36.43, -50.85) * mm]});
            skFitSpline(sketch, "E735", {"points": [v(-36.43, -50.85) * mm, v(-35.17, -49.52) * mm, v(-33.74, -48.4) * mm, v(-31.76, -48.38) * mm]});
            skFitSpline(sketch, "E736", {"points": [v(75.51, -36.93) * mm, v(74.78, -37.89) * mm, v(74.29, -38.72) * mm, v(73.61, -39.37) * mm]});
            skFitSpline(sketch, "E737", {"points": [v(73.61, -39.37) * mm, v(72.94, -40.03) * mm, v(72.09, -40.52) * mm, v(71.3, -41.06) * mm]});
            skFitSpline(sketch, "E738", {"points": [v(71.3, -41.06) * mm, v(69.86, -42.07) * mm, v(68.72, -43.31) * mm, v(68.14, -45.03) * mm]});
            skFitSpline(sketch, "E739", {"points": [v(68.14, -45.03) * mm, v(67.94, -45.64) * mm, v(67.65, -46.24) * mm, v(67.4, -46.85) * mm]});
            skFitSpline(sketch, "E740", {"points": [v(67.4, -46.85) * mm, v(66.2, -46.85) * mm, v(65.27, -46.85) * mm, v(64.95, -46.85) * mm]});
            skFitSpline(sketch, "E741", {"points": [v(64.95, -46.85) * mm, v(64.52, -46.84) * mm, v(64.11, -46.95) * mm, v(63.89, -47.68) * mm]});
            skFitSpline(sketch, "E742", {"points": [v(63.89, -47.68) * mm, v(64.93, -47.68) * mm, v(67.06, -47.7) * mm, v(67.17, -47.73) * mm]});
            skFitSpline(sketch, "E743", {"points": [v(67.17, -47.73) * mm, v(67.08, -48.17) * mm, v(67.02, -48.54) * mm, v(66.92, -48.9) * mm]});
            skFitSpline(sketch, "E744", {"points": [v(66.92, -48.9) * mm, v(65.74, -53.03) * mm, v(64.54, -57.16) * mm, v(63.36, -61.3) * mm]});
            skFitSpline(sketch, "E745", {"points": [v(63.36, -61.3) * mm, v(62.76, -63.41) * mm, v(62.13, -65.52) * mm, v(61.61, -67.65) * mm]});
            skFitSpline(sketch, "E746", {"points": [v(61.61, -67.65) * mm, v(61.03, -70.06) * mm, v(61.83, -72.15) * mm, v(63.95, -73.31) * mm]});
            skFitSpline(sketch, "E747", {"points": [v(63.95, -73.31) * mm, v(67.87, -75.46) * mm, v(71.92, -74.6) * mm, v(74.04, -70.87) * mm]});
            skFitSpline(sketch, "E748", {"points": [v(75.14, -67.6) * mm, v(74.41, -68.21) * mm, v(74.46, -68.23) * mm, v(74.28, -68.84) * mm]});
            skFitSpline(sketch, "E749", {"points": [v(74.28, -68.84) * mm, v(74.08, -69.5) * mm, v(73.84, -70.1) * mm, v(73.55, -70.67) * mm]});
            skFitSpline(sketch, "E750", {"points": [v(73.55, -70.67) * mm, v(72.56, -72.21) * mm, v(71.22, -73.38) * mm, v(69.21, -73.85) * mm]});
            skFitSpline(sketch, "E751", {"points": [v(69.21, -73.85) * mm, v(67.52, -74.25) * mm, v(66.3, -73.4) * mm, v(66.29, -71.66) * mm]});
            skFitSpline(sketch, "E752", {"points": [v(66.29, -71.66) * mm, v(66.28, -70.53) * mm, v(66.44, -69.36) * mm, v(66.74, -68.27) * mm]});
            skFitSpline(sketch, "E753", {"points": [v(66.74, -68.27) * mm, v(68.32, -62.61) * mm, v(69.96, -56.97) * mm, v(71.6, -51.32) * mm]});
            skFitSpline(sketch, "E754", {"points": [v(71.6, -51.32) * mm, v(71.94, -50.13) * mm, v(72.33, -48.95) * mm, v(72.73, -47.68) * mm]});
            skLineSegment(sketch, "E755", {"start": v(72.73, -47.68) * mm, "end": v(78.84, -47.68) * mm});
            skFitSpline(sketch, "E756", {"points": [v(78.84, -47.68) * mm, v(79.12, -47.4) * mm, v(79.1, -47.14) * mm, v(79.37, -46.87) * mm]});
            skFitSpline(sketch, "E757", {"points": [v(79.37, -46.87) * mm, v(78.74, -46.86) * mm, v(75.7, -46.86) * mm, v(72.9, -46.85) * mm]});
            skFitSpline(sketch, "E758", {"points": [v(72.9, -46.85) * mm, v(73.2, -45.85) * mm, v(73.44, -45.07) * mm, v(73.66, -44.29) * mm]});
            skFitSpline(sketch, "E759", {"points": [v(73.66, -44.29) * mm, v(73.88, -43.5) * mm, v(74.1, -42.72) * mm, v(74.31, -41.94) * mm]});
            skFitSpline(sketch, "E760", {"points": [v(74.31, -41.94) * mm, v(74.55, -41.11) * mm, v(74.82, -40.3) * mm, v(75.03, -39.46) * mm]});
            skFitSpline(sketch, "E761", {"points": [v(75.03, -39.46) * mm, v(75.21, -38.7) * mm, v(75.65, -37.95) * mm, v(75.51, -36.93) * mm]});
            skFitSpline(sketch, "E762", {"points": [v(82.84, -46.84) * mm, v(82.4, -46.84) * mm, v(82, -46.95) * mm, v(81.78, -47.67) * mm]});
            skLineSegment(sketch, "E763", {"start": v(81.78, -47.67) * mm, "end": v(87.92, -47.67) * mm});
            skFitSpline(sketch, "E764", {"points": [v(87.92, -47.67) * mm, v(86.3, -48.64) * mm, v(85.2, -49.9) * mm, v(84.68, -51.64) * mm]});
            skFitSpline(sketch, "E765", {"points": [v(84.68, -51.64) * mm, v(83.18, -56.68) * mm, v(81.7, -61.72) * mm, v(80.24, -66.77) * mm]});
            skFitSpline(sketch, "E766", {"points": [v(80.24, -66.77) * mm, v(79.88, -68.03) * mm, v(79.84, -69.33) * mm, v(80.25, -70.6) * mm]});
            skFitSpline(sketch, "E767", {"points": [v(80.25, -70.6) * mm, v(81.18, -73.51) * mm, v(84.49, -75.11) * mm, v(87.72, -74.28) * mm]});
            skFitSpline(sketch, "E768", {"points": [v(87.72, -74.28) * mm, v(90.5, -73.56) * mm, v(92.52, -71.78) * mm, v(94.3, -69.66) * mm]});
            skFitSpline(sketch, "E769", {"points": [v(94.3, -69.66) * mm, v(95, -68.83) * mm, v(95.63, -67.94) * mm, v(96.5, -66.81) * mm]});
            skFitSpline(sketch, "E770", {"points": [v(96.5, -66.81) * mm, v(96.38, -67.51) * mm, v(96.3, -67.88) * mm, v(96.26, -68.25) * mm]});
            skFitSpline(sketch, "E771", {"points": [v(96.26, -68.25) * mm, v(96.05, -69.86) * mm, v(96.42, -71.3) * mm, v(97.56, -72.48) * mm]});
            skFitSpline(sketch, "E772", {"points": [v(97.56, -72.48) * mm, v(100.48, -75.51) * mm, v(105.87, -75.13) * mm, v(108.32, -71.72) * mm]});
            skFitSpline(sketch, "E773", {"points": [v(108.32, -71.72) * mm, v(108.71, -71.17) * mm, v(109.02, -70.59) * mm, v(109.31, -69.99) * mm]});
            skFitSpline(sketch, "E774", {"points": [v(109.98, -67.55) * mm, v(109.19, -68.2) * mm, v(109.19, -68.2) * mm, v(109.04, -68.89) * mm]});
            skFitSpline(sketch, "E775", {"points": [v(109.04, -68.89) * mm, v(108.88, -69.6) * mm, v(108.64, -70.03) * mm, v(108.4, -70.55) * mm]});
            skFitSpline(sketch, "E776", {"points": [v(108.4, -70.55) * mm, v(108.05, -71.13) * mm, v(107.65, -71.67) * mm, v(107.18, -72.16) * mm]});
            skFitSpline(sketch, "E777", {"points": [v(107.18, -72.16) * mm, v(106.15, -73.2) * mm, v(104.95, -73.97) * mm, v(103.4, -73.98) * mm]});
            skFitSpline(sketch, "E778", {"points": [v(103.4, -73.98) * mm, v(102, -74) * mm, v(101.2, -73.38) * mm, v(101.1, -71.99) * mm]});
            skFitSpline(sketch, "E779", {"points": [v(101.1, -71.99) * mm, v(101.04, -71.1) * mm, v(101.06, -70.15) * mm, v(101.3, -69.3) * mm]});
            skFitSpline(sketch, "E780", {"points": [v(101.3, -69.3) * mm, v(102.9, -63.49) * mm, v(104.57, -57.7) * mm, v(106.22, -51.9) * mm]});
            skFitSpline(sketch, "E781", {"points": [v(106.22, -51.9) * mm, v(106.66, -50.36) * mm, v(107.09, -48.8) * mm, v(107.58, -47.04) * mm]});
            skFitSpline(sketch, "E782", {"points": [v(107.58, -47.04) * mm, v(105.7, -46.9) * mm, v(104.07, -46.9) * mm, v(102.43, -47.04) * mm]});
            skFitSpline(sketch, "E783", {"points": [v(102.43, -47.04) * mm, v(102.26, -47.46) * mm, v(99.78, -55.68) * mm, v(98.72, -59.5) * mm]});
            skFitSpline(sketch, "E784", {"points": [v(98.72, -59.5) * mm, v(97.43, -64.17) * mm, v(95.31, -68.33) * mm, v(91.63, -71.58) * mm]});
            skFitSpline(sketch, "E785", {"points": [v(91.63, -71.58) * mm, v(90.4, -72.68) * mm, v(88.97, -73.47) * mm, v(87.37, -73.84) * mm]});
            skFitSpline(sketch, "E786", {"points": [v(87.37, -73.84) * mm, v(86.26, -74.1) * mm, v(85.07, -74.33) * mm, v(84.1, -72.93) * mm]});
            skFitSpline(sketch, "E787", {"points": [v(84.1, -72.93) * mm, v(83.93, -72.38) * mm, v(84.17, -71.59) * mm, v(84.37, -70.87) * mm]});
            skFitSpline(sketch, "E788", {"points": [v(84.37, -70.87) * mm, v(86.5, -63.48) * mm, v(91.15, -46.92) * mm, v(91.2, -46.85) * mm]});
            skFitSpline(sketch, "E789", {"points": [v(91.2, -46.85) * mm, v(89.37, -46.85) * mm, v(83.28, -46.84) * mm, v(82.84, -46.84) * mm]});
            skFitSpline(sketch, "E790", {"points": [v(134.97, -33.58) * mm, v(134.53, -33.58) * mm, v(134.13, -33.7) * mm, v(133.9, -34.42) * mm]});
            skLineSegment(sketch, "E791", {"start": v(133.9, -34.42) * mm, "end": v(141.76, -34.42) * mm});
            skFitSpline(sketch, "E792", {"points": [v(141.76, -34.42) * mm, v(140.31, -35.74) * mm, v(139.74, -37.23) * mm, v(139.3, -38.79) * mm]});
            skFitSpline(sketch, "E793", {"points": [v(139.3, -38.79) * mm, v(138.22, -42.6) * mm, v(137.16, -46.43) * mm, v(136.08, -50.24) * mm]});
            skFitSpline(sketch, "E794", {"points": [v(136.08, -50.24) * mm, v(135.87, -51) * mm, v(135.63, -51.74) * mm, v(135.4, -52.5) * mm]});
            skFitSpline(sketch, "E795", {"points": [v(135.4, -52.5) * mm, v(135.1, -52.08) * mm, v(135.08, -51.72) * mm, v(135.05, -51.36) * mm]});
            skFitSpline(sketch, "E796", {"points": [v(135.05, -51.36) * mm, v(134.75, -48.4) * mm, v(132.85, -46.7) * mm, v(129.92, -46.68) * mm]});
            skFitSpline(sketch, "E797", {"points": [v(129.92, -46.68) * mm, v(126.68, -46.66) * mm, v(123.97, -48.02) * mm, v(121.57, -50.01) * mm]});
            skFitSpline(sketch, "E798", {"points": [v(121.57, -50.01) * mm, v(117.7, -53.23) * mm, v(115.23, -57.37) * mm, v(113.86, -62.2) * mm]});
            skFitSpline(sketch, "E799", {"points": [v(113.86, -62.2) * mm, v(113.31, -64.12) * mm, v(113.24, -66.08) * mm, v(113.46, -68.04) * mm]});
            skFitSpline(sketch, "E800", {"points": [v(113.46, -68.04) * mm, v(113.65, -69.68) * mm, v(114.32, -71.17) * mm, v(115.52, -72.36) * mm]});
            skFitSpline(sketch, "E801", {"points": [v(115.52, -72.36) * mm, v(117.92, -74.77) * mm, v(122.12, -75.25) * mm, v(125.08, -73.44) * mm]});
            skFitSpline(sketch, "E802", {"points": [v(125.08, -73.44) * mm, v(127.16, -72.18) * mm, v(128.79, -70.44) * mm, v(130.18, -68.46) * mm]});
            skFitSpline(sketch, "E803", {"points": [v(130.18, -68.46) * mm, v(130.4, -68.15) * mm, v(130.66, -67.85) * mm, v(130.9, -67.55) * mm]});
            skFitSpline(sketch, "E804", {"points": [v(130.9, -67.55) * mm, v(131.08, -68) * mm, v(131.04, -68.33) * mm, v(131.03, -68.65) * mm]});
            skFitSpline(sketch, "E805", {"points": [v(131.03, -68.65) * mm, v(130.95, -70.5) * mm, v(131.6, -72.05) * mm, v(133.12, -73.13) * mm]});
            skFitSpline(sketch, "E806", {"points": [v(133.12, -73.13) * mm, v(135.12, -74.55) * mm, v(137.4, -74.9) * mm, v(139.7, -74.24) * mm]});
            skFitSpline(sketch, "E807", {"points": [v(139.7, -74.24) * mm, v(141.72, -73.66) * mm, v(143.54, -71.6) * mm, v(144.36, -69.32) * mm]});
            skFitSpline(sketch, "E808", {"points": [v(144.06, -68.57) * mm, v(143.65, -69.8) * mm, v(143.08, -70.93) * mm, v(142.22, -71.9) * mm]});
            skFitSpline(sketch, "E809", {"points": [v(142.22, -71.9) * mm, v(141.1, -73.15) * mm, v(139.77, -74.04) * mm, v(138, -73.98) * mm]});
            skFitSpline(sketch, "E810", {"points": [v(138, -73.98) * mm, v(136.89, -73.94) * mm, v(136.25, -73.52) * mm, v(136.05, -72.43) * mm]});
            skFitSpline(sketch, "E811", {"points": [v(136.05, -72.43) * mm, v(135.89, -71.56) * mm, v(135.82, -70.6) * mm, v(136.02, -69.74) * mm]});
            skFitSpline(sketch, "E812", {"points": [v(136.02, -69.74) * mm, v(136.74, -66.72) * mm, v(137.56, -63.73) * mm, v(138.4, -60.73) * mm]});
            skFitSpline(sketch, "E813", {"points": [v(138.4, -60.73) * mm, v(140.22, -54.15) * mm, v(146.04, -33.87) * mm, v(146.32, -33.6) * mm]});
            skFitSpline(sketch, "E814", {"points": [v(146.32, -33.6) * mm, v(145.18, -33.6) * mm, v(136.11, -33.59) * mm, v(134.97, -33.58) * mm]});
            skFitSpline(sketch, "E815", {"points": [v(130.4, -47.26) * mm, v(132.74, -47.24) * mm, v(134.11, -48.69) * mm, v(134.61, -51.59) * mm]});
            skFitSpline(sketch, "E816", {"points": [v(134.61, -51.59) * mm, v(134.72, -52.19) * mm, v(134.63, -52.83) * mm, v(134.63, -53.45) * mm]});
            skFitSpline(sketch, "E817", {"points": [v(134.63, -53.45) * mm, v(134.8, -56.25) * mm, v(133.53, -58.74) * mm, v(132.9, -61.37) * mm]});
            skFitSpline(sketch, "E818", {"points": [v(132.9, -61.37) * mm, v(132.06, -64.91) * mm, v(130.23, -67.9) * mm, v(127.75, -70.5) * mm]});
            skFitSpline(sketch, "E819", {"points": [v(127.75, -70.5) * mm, v(126.53, -71.8) * mm, v(125.14, -72.88) * mm, v(123.49, -73.6) * mm]});
            skFitSpline(sketch, "E820", {"points": [v(123.49, -73.6) * mm, v(121.16, -74.63) * mm, v(119.2, -73.7) * mm, v(118.47, -71.24) * mm]});
            skFitSpline(sketch, "E821", {"points": [v(118.47, -71.24) * mm, v(117.9, -69.3) * mm, v(118.06, -67.33) * mm, v(118.37, -65.4) * mm]});
            skFitSpline(sketch, "E822", {"points": [v(118.37, -65.4) * mm, v(119.12, -60.78) * mm, v(120.73, -56.44) * mm, v(123.32, -52.52) * mm]});
            skFitSpline(sketch, "E823", {"points": [v(123.32, -52.52) * mm, v(124.26, -51.1) * mm, v(125.45, -49.82) * mm, v(126.7, -48.66) * mm]});
            skFitSpline(sketch, "E824", {"points": [v(126.7, -48.66) * mm, v(127.4, -48.01) * mm, v(128.4, -47.52) * mm, v(129.35, -47.36) * mm]});
            skFitSpline(sketch, "E825", {"points": [v(129.35, -47.36) * mm, v(129.72, -47.3) * mm, v(130.07, -47.26) * mm, v(130.4, -47.26) * mm]});
            skFitSpline(sketch, "E826", {"points": [v(163.14, -67.56) * mm, v(162.62, -67.98) * mm, v(162.52, -68.1) * mm, v(162.43, -68.37) * mm]});
            skLineSegment(sketch, "E827", {"start": v(162.43, -68.37) * mm, "end": v(162.43, -68.37) * mm});
            skFitSpline(sketch, "E828", {"points": [v(162.43, -68.37) * mm, v(161.59, -70.92) * mm, v(160.22, -73) * mm, v(157.41, -73.78) * mm]});
            skFitSpline(sketch, "E829", {"points": [v(157.41, -73.78) * mm, v(155.29, -74.38) * mm, v(154.1, -73.5) * mm, v(154.2, -71.3) * mm]});
            skFitSpline(sketch, "E830", {"points": [v(154.2, -71.3) * mm, v(154.28, -69.93) * mm, v(154.58, -68.55) * mm, v(154.95, -67.22) * mm]});
            skFitSpline(sketch, "E831", {"points": [v(154.95, -67.22) * mm, v(156.72, -60.97) * mm, v(160.65, -47) * mm, v(160.7, -46.95) * mm]});
            skFitSpline(sketch, "E832", {"points": [v(160.7, -46.95) * mm, v(159.56, -46.94) * mm, v(153.39, -46.93) * mm, v(152.24, -46.93) * mm]});
            skFitSpline(sketch, "E833", {"points": [v(152.24, -46.93) * mm, v(151.8, -46.93) * mm, v(151.4, -47.04) * mm, v(151.18, -47.76) * mm]});
            skLineSegment(sketch, "E834", {"start": v(151.18, -47.76) * mm, "end": v(157.4, -47.76) * mm});
            skFitSpline(sketch, "E835", {"points": [v(157.4, -47.76) * mm, v(155.27, -48.86) * mm, v(154.34, -50.78) * mm, v(153.73, -52.95) * mm]});
            skFitSpline(sketch, "E836", {"points": [v(153.73, -52.95) * mm, v(153.15, -55.03) * mm, v(152.56, -57.1) * mm, v(151.96, -59.16) * mm]});
            skFitSpline(sketch, "E837", {"points": [v(151.96, -59.16) * mm, v(151.13, -62.06) * mm, v(150.24, -64.93) * mm, v(149.5, -67.85) * mm]});
            skFitSpline(sketch, "E838", {"points": [v(149.5, -67.85) * mm, v(148.97, -69.88) * mm, v(149.61, -71.63) * mm, v(151.25, -72.97) * mm]});
            skFitSpline(sketch, "E839", {"points": [v(151.25, -72.97) * mm, v(153.24, -74.6) * mm, v(156.97, -75) * mm, v(159.13, -73.67) * mm]});
            skFitSpline(sketch, "E840", {"points": [v(159.13, -73.67) * mm, v(160.95, -72.54) * mm, v(162.14, -71.02) * mm, v(162.76, -69.08) * mm]});
            skLineSegment(sketch, "E841", {"start": v(-58.05, -74.75) * mm, "end": v(-57.4, -74.44) * mm});
            skLineSegment(sketch, "E842", {"start": v(-57.68, -75.29) * mm, "end": v(-57, -75) * mm});
            skLineSegment(sketch, "E843", {"start": v(74.04, -70.87) * mm, "end": v(75.19, -68.3) * mm});
            skLineSegment(sketch, "E844", {"start": v(75.19, -68.3) * mm, "end": v(75.14, -67.6) * mm});
            skLineSegment(sketch, "E845", {"start": v(109.31, -69.99) * mm, "end": v(109.68, -68.9) * mm});
            skLineSegment(sketch, "E846", {"start": v(109.68, -68.9) * mm, "end": v(109.86, -68.25) * mm});
            skLineSegment(sketch, "E847", {"start": v(109.86, -68.25) * mm, "end": v(109.98, -67.55) * mm});
            skLineSegment(sketch, "E848", {"start": v(144.06, -68.57) * mm, "end": v(144.18, -68.29) * mm});
            skLineSegment(sketch, "E849", {"start": v(144.18, -68.29) * mm, "end": v(144.31, -68.06) * mm});
            skLineSegment(sketch, "E850", {"start": v(144.31, -68.06) * mm, "end": v(144.48, -67.87) * mm});
            skLineSegment(sketch, "E851", {"start": v(144.48, -67.87) * mm, "end": v(144.78, -67.65) * mm});
            skLineSegment(sketch, "E852", {"start": v(144.36, -69.32) * mm, "end": v(144.78, -67.65) * mm});
            skLineSegment(sketch, "E853", {"start": v(163.14, -67.56) * mm, "end": v(162.76, -69.08) * mm});
            skSolve(sketch);
        }
        {
            var Q0;
            Q0 = qSketchRegion(id + "F6", true);
            extrude(context, id + "F7", {"entities" : qUnion([Q0]), "depth" : 50 * mm, "offsetDistance" : 25 * mm});
        }
        {
            var Q0;
            Q0=makeQuery(id+"F5.opExtrude","SWEPT_BODY",BODY,{"disambiguationData":[OSD([sQuery(id+"F4.wireOp",EDGE,"E477.bottom"),sQuery(id+"F4.wireOp",EDGE,"E477.top"),sQuery(id+"F4.wireOp",EDGE,"E477.left"),sQuery(id+"F4.wireOp",EDGE,"E477.right")])]});
            deleteBodies(context, id + "F8", {"entities" : qUnion([Q0])});
        }
        {
            var Q0;
            Q0=makeQuery(id+"F3.opExtrude","CAP_FACE",FACE,{"disambiguationData":[OSD([sQuery(id+"F2.wireOp",EDGE,"E476.bottom"),sQuery(id+"F2.wireOp",EDGE,"E476.top"),sQuery(id+"F2.wireOp",EDGE,"E476.left"),sQuery(id+"F2.wireOp",EDGE,"E476.right")])],"isStart":true});
            var sketch = newSketch(context, id + "F9", { "sketchPlane" : qUnion([Q0])});
            skLineSegment(sketch, "E854.bottom", {"start": v(-23.28, -86.25) * mm, "end": v(23.13, -86.25) * mm});
            skLineSegment(sketch, "E854.top", {"start": v(-23.28, -76.4) * mm, "end": v(23.13, -76.4) * mm});
            skLineSegment(sketch, "E854.left", {"start": v(-23.28, -86.25) * mm, "end": v(-23.28, -76.4) * mm});
            skLineSegment(sketch, "E854.right", {"start": v(23.13, -86.25) * mm, "end": v(23.13, -76.4) * mm});
            skSolve(sketch);
        }
        {
            var Q0;
            Q0 = qSketchRegion(id + "F9", true);
            extrude(context, id + "F10", {"entities" : qUnion([Q0]), "operationType" : NewBodyOperationType.ADD, "depth" : 25 * mm, "offsetDistance" : 25 * mm});
        }
        {
            var Q0;
            Q0=makeQuery(id+"F10.opExtrude","CAP_EDGE",EDGE,{"disambiguationData":[OSD([sQuery(id+"F9.wireOp",EDGE,"E854.top")])],"isStart":false});
            var Q1;
            Q1=makeQuery(id+"F10.opExtrude","SWEPT_EDGE",EDGE,{"disambiguationData":[OSD([sQuery(id+"F9.wireOp",EDGE,"E854.top"),sQuery(id+"F9.wireOp",EDGE,"E854.right")])]});
            var Q2;
            Q2=makeQuery(id+"F10.opExtrude","SWEPT_EDGE",EDGE,{"disambiguationData":[OSD([sQuery(id+"F9.wireOp",EDGE,"E854.top"),sQuery(id+"F9.wireOp",EDGE,"E854.left")])]});
            fillet(context, id + "F11", {"entities" : qUnion([Q0, Q1, Q2]), "radius" : 5 * mm, "tangentPropagation" : true, "allowEdgeOverflow" : false});
        }
    });
